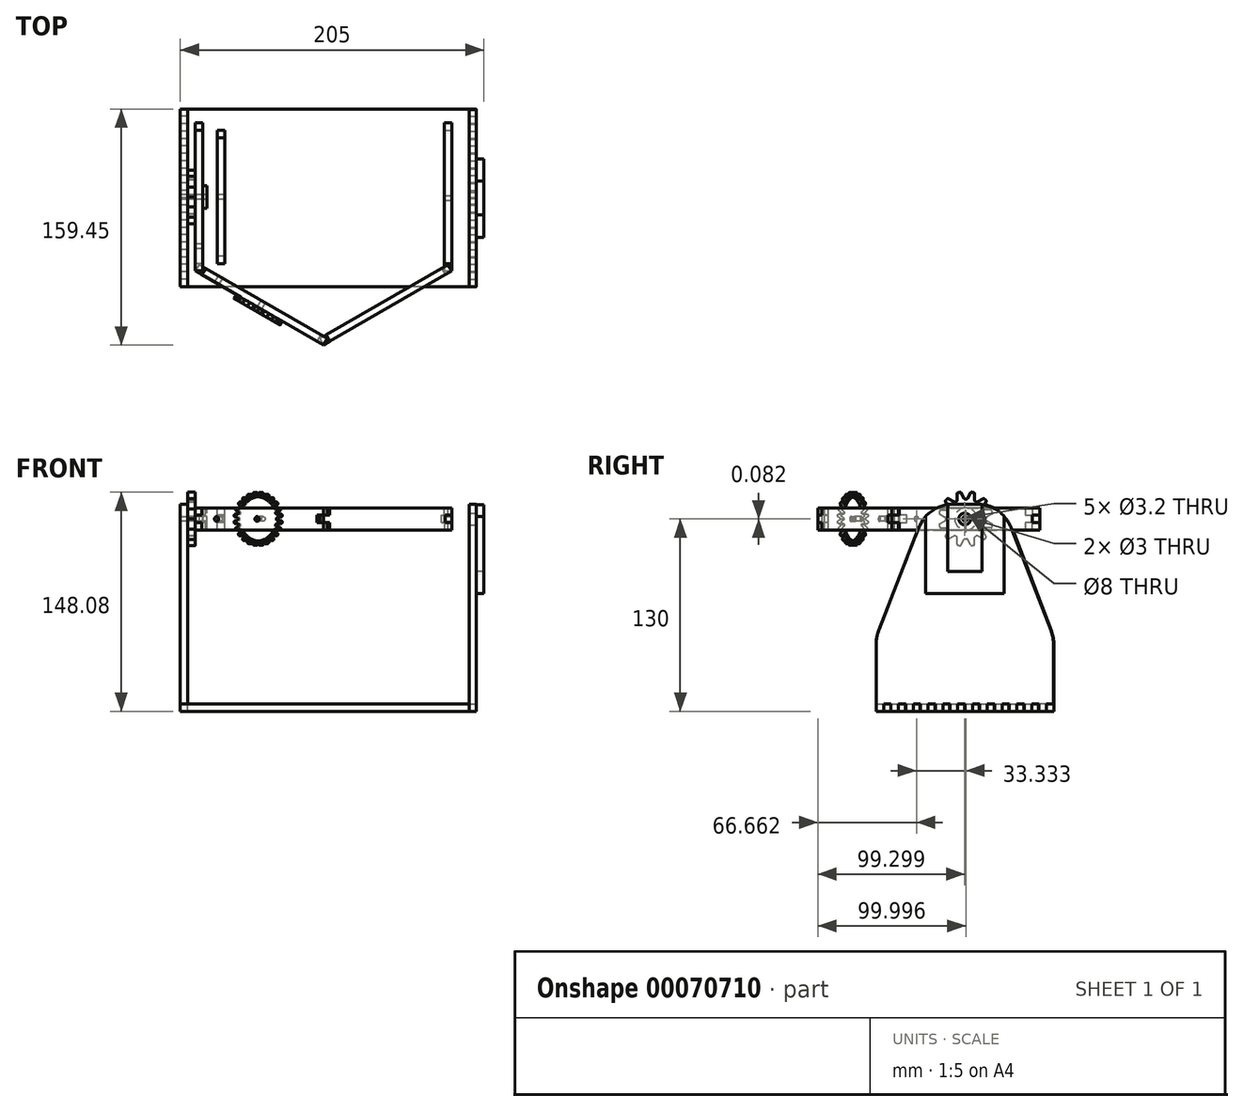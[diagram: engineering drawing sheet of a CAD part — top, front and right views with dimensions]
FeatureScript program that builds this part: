
annotation { "Feature Type Name" : "Feature", "Feature Type Description" : "" }
export const myFeature = defineFeature(function(context is Context, id is Id, definition is map)
    precondition{}
    {
        {
            var Q0;
            Q0=qCreatedBy(makeId("Top.planeOp"),FACE);
            var sketch = newSketch(context, id + "F0", { "sketchPlane" : qUnion([Q0])});
            skLineSegment(sketch, "E0.rect.bottom", {"start": v(100, 60) * mm, "end": v(-95, 60) * mm});
            skLineSegment(sketch, "E0.rect.top", {"start": v(95, -60) * mm, "end": v(-100, -60) * mm});
            skLineSegment(sketch, "E0.rect.left", {"start": v(100, 60) * mm, "end": v(100, 55) * mm});
            skLineSegment(sketch, "E0.rect.right", {"start": v(-100, 55) * mm, "end": v(-100, 50) * mm});
            skPoint(sketch, "E0.rect.middle", {"position": v(0, 0) * mm});
            skLineSegment(sketch, "E1.bottom", {"start": v(100, 55) * mm, "end": v(95, 55) * mm});
            skLineSegment(sketch, "E1.top", {"start": v(100, 50) * mm, "end": v(95, 50) * mm});
            skLineSegment(sketch, "E1.right", {"start": v(95, 55) * mm, "end": v(95, 50) * mm});
            skLineSegment(sketch, "E2.0.1.0", {"start": v(100, 45) * mm, "end": v(95, 45) * mm});
            skLineSegment(sketch, "E2.0.1.1", {"start": v(95, 45) * mm, "end": v(95, 40) * mm});
            skLineSegment(sketch, "E2.0.1.2", {"start": v(100, 40) * mm, "end": v(95, 40) * mm});
            skLineSegment(sketch, "E2.0.2.0", {"start": v(100, 35) * mm, "end": v(95, 35) * mm});
            skLineSegment(sketch, "E2.0.2.1", {"start": v(95, 35) * mm, "end": v(95, 30) * mm});
            skLineSegment(sketch, "E2.0.2.2", {"start": v(100, 30) * mm, "end": v(95, 30) * mm});
            skLineSegment(sketch, "E2.0.3.0", {"start": v(100, 25) * mm, "end": v(95, 25) * mm});
            skLineSegment(sketch, "E2.0.3.1", {"start": v(95, 25) * mm, "end": v(95, 20) * mm});
            skLineSegment(sketch, "E2.0.3.2", {"start": v(100, 20) * mm, "end": v(95, 20) * mm});
            skLineSegment(sketch, "E2.0.4.0", {"start": v(100, 15) * mm, "end": v(95, 15) * mm});
            skLineSegment(sketch, "E2.0.4.1", {"start": v(95, 15) * mm, "end": v(95, 10) * mm});
            skLineSegment(sketch, "E2.0.4.2", {"start": v(100, 10) * mm, "end": v(95, 10) * mm});
            skLineSegment(sketch, "E2.0.5.0", {"start": v(100, 5) * mm, "end": v(95, 5) * mm});
            skLineSegment(sketch, "E2.0.5.1", {"start": v(95, 5) * mm, "end": v(95, 0) * mm});
            skLineSegment(sketch, "E2.0.5.2", {"start": v(100, 0) * mm, "end": v(95, 0) * mm});
            skLineSegment(sketch, "E2.0.6.0", {"start": v(100, -5) * mm, "end": v(95, -5) * mm});
            skLineSegment(sketch, "E2.0.6.1", {"start": v(95, -5) * mm, "end": v(95, -10) * mm});
            skLineSegment(sketch, "E2.0.6.2", {"start": v(100, -10) * mm, "end": v(95, -10) * mm});
            skLineSegment(sketch, "E2.0.7.0", {"start": v(100, -15) * mm, "end": v(95, -15) * mm});
            skLineSegment(sketch, "E2.0.7.1", {"start": v(95, -15) * mm, "end": v(95, -20) * mm});
            skLineSegment(sketch, "E2.0.7.2", {"start": v(100, -20) * mm, "end": v(95, -20) * mm});
            skLineSegment(sketch, "E2.0.8.0", {"start": v(100, -25) * mm, "end": v(95, -25) * mm});
            skLineSegment(sketch, "E2.0.8.1", {"start": v(95, -25) * mm, "end": v(95, -30) * mm});
            skLineSegment(sketch, "E2.0.8.2", {"start": v(100, -30) * mm, "end": v(95, -30) * mm});
            skLineSegment(sketch, "E2.0.9.0", {"start": v(100, -35) * mm, "end": v(95, -35) * mm});
            skLineSegment(sketch, "E2.0.9.1", {"start": v(95, -35) * mm, "end": v(95, -40) * mm});
            skLineSegment(sketch, "E2.0.9.2", {"start": v(100, -40) * mm, "end": v(95, -40) * mm});
            skLineSegment(sketch, "E2.0.10.0", {"start": v(100, -45) * mm, "end": v(95, -45) * mm});
            skLineSegment(sketch, "E2.0.10.1", {"start": v(95, -45) * mm, "end": v(95, -50) * mm});
            skLineSegment(sketch, "E2.0.10.2", {"start": v(100, -50) * mm, "end": v(95, -50) * mm});
            skLineSegment(sketch, "E2.0.11.0", {"start": v(100, -55) * mm, "end": v(95, -55) * mm});
            skLineSegment(sketch, "E2.0.11.1", {"start": v(95, -55) * mm, "end": v(95, -60) * mm});
            skLineSegment(sketch, "E2.direction1", {"start": v(95, 55) * mm, "end": v(119, 55) * mm, "construction": true});
            skLineSegment(sketch, "E2.direction2", {"start": v(95, 55) * mm, "end": v(95, 45) * mm, "construction": true});
            skLineSegment(sketch, "E3", {"start": v(0, -60) * mm, "end": v(0, 60) * mm, "construction": true});
            skLineSegment(sketch, "E4.1.0", {"start": v(-100, -30) * mm, "end": v(-95, -30) * mm});
            skLineSegment(sketch, "E4.1.1", {"start": v(-100, 15) * mm, "end": v(-95, 15) * mm});
            skLineSegment(sketch, "E4.1.2", {"start": v(-95, -35) * mm, "end": v(-95, -30) * mm});
            skLineSegment(sketch, "E4.1.3", {"start": v(-100, 30) * mm, "end": v(-95, 30) * mm});
            skLineSegment(sketch, "E4.1.4", {"start": v(-100, 0) * mm, "end": v(-95, 0) * mm});
            skLineSegment(sketch, "E4.1.5", {"start": v(-100, 55) * mm, "end": v(-95, 55) * mm});
            skLineSegment(sketch, "E4.1.6", {"start": v(-95, 55) * mm, "end": v(-95, 60) * mm});
            skLineSegment(sketch, "E4.1.7", {"start": v(-100, -25) * mm, "end": v(-95, -25) * mm});
            skLineSegment(sketch, "E4.1.8", {"start": v(-100, 5) * mm, "end": v(-95, 5) * mm});
            skLineSegment(sketch, "E4.1.9", {"start": v(-95, -25) * mm, "end": v(-95, -20) * mm});
            skLineSegment(sketch, "E4.1.10", {"start": v(-100, 35) * mm, "end": v(-95, 35) * mm});
            skLineSegment(sketch, "E4.1.11", {"start": v(-100, -20) * mm, "end": v(-95, -20) * mm});
            skLineSegment(sketch, "E4.1.12", {"start": v(-100, -35) * mm, "end": v(-95, -35) * mm});
            skLineSegment(sketch, "E4.1.13", {"start": v(-100, -40) * mm, "end": v(-95, -40) * mm});
            skLineSegment(sketch, "E4.1.14", {"start": v(-95, -45) * mm, "end": v(-95, -40) * mm});
            skLineSegment(sketch, "E4.1.15", {"start": v(-95, -55) * mm, "end": v(-95, -50) * mm});
            skLineSegment(sketch, "E4.1.16", {"start": v(-95, 25) * mm, "end": v(-95, 30) * mm});
            skLineSegment(sketch, "E4.1.17", {"start": v(-100, 50) * mm, "end": v(-95, 50) * mm});
            skLineSegment(sketch, "E4.1.18", {"start": v(-95, -5) * mm, "end": v(-95, 0) * mm});
            skLineSegment(sketch, "E4.1.19", {"start": v(-100, 20) * mm, "end": v(-95, 20) * mm});
            skLineSegment(sketch, "E4.1.20", {"start": v(-95, 45) * mm, "end": v(-95, 50) * mm});
            skLineSegment(sketch, "E4.1.21", {"start": v(-100, 25) * mm, "end": v(-95, 25) * mm});
            skLineSegment(sketch, "E4.1.22", {"start": v(-100, 40) * mm, "end": v(-95, 40) * mm});
            skLineSegment(sketch, "E4.1.23", {"start": v(-100, -5) * mm, "end": v(-95, -5) * mm});
            skLineSegment(sketch, "E4.1.24", {"start": v(-95, 15) * mm, "end": v(-95, 20) * mm});
            skLineSegment(sketch, "E4.1.25", {"start": v(-95, -15) * mm, "end": v(-95, -10) * mm});
            skLineSegment(sketch, "E4.1.26", {"start": v(-100, 10) * mm, "end": v(-95, 10) * mm});
            skLineSegment(sketch, "E4.1.27", {"start": v(-95, 35) * mm, "end": v(-95, 40) * mm});
            skLineSegment(sketch, "E4.1.28", {"start": v(-100, 45) * mm, "end": v(-95, 45) * mm});
            skLineSegment(sketch, "E4.1.29", {"start": v(-100, -10) * mm, "end": v(-95, -10) * mm});
            skLineSegment(sketch, "E4.1.30", {"start": v(-100, -15) * mm, "end": v(-95, -15) * mm});
            skLineSegment(sketch, "E4.1.31", {"start": v(-95, 5) * mm, "end": v(-95, 10) * mm});
            skLineSegment(sketch, "E4.1.32", {"start": v(-100, -45) * mm, "end": v(-95, -45) * mm});
            skLineSegment(sketch, "E4.1.33", {"start": v(-100, -50) * mm, "end": v(-95, -50) * mm});
            skLineSegment(sketch, "E4.1.35", {"start": v(-100, -55) * mm, "end": v(-95, -55) * mm});
            skLineSegment(sketch, "E4.anchor1", {"start": v(0, 0) * mm, "end": v(95, 30) * mm, "construction": true});
            skLineSegment(sketch, "E4.anchor2", {"start": v(0, 0) * mm, "end": v(-95, -30) * mm, "construction": true});
            skLineSegment(sketch, "E5.trimOffspring", {"start": v(100, 50) * mm, "end": v(100, 45) * mm});
            skLineSegment(sketch, "E6.trimOffspring", {"start": v(100, 40) * mm, "end": v(100, 35) * mm});
            skLineSegment(sketch, "E7.trimOffspring", {"start": v(100, 30) * mm, "end": v(100, 25) * mm});
            skLineSegment(sketch, "E8.trimOffspring", {"start": v(100, 20) * mm, "end": v(100, 15) * mm});
            skLineSegment(sketch, "E9.trimOffspring", {"start": v(100, 10) * mm, "end": v(100, 5) * mm});
            skLineSegment(sketch, "E10.trimOffspring", {"start": v(100, 0) * mm, "end": v(100, -5) * mm});
            skLineSegment(sketch, "E11.trimOffspring", {"start": v(100, -10) * mm, "end": v(100, -15) * mm});
            skLineSegment(sketch, "E12.trimOffspring", {"start": v(100, -20) * mm, "end": v(100, -25) * mm});
            skLineSegment(sketch, "E13.trimOffspring", {"start": v(100, -30) * mm, "end": v(100, -35) * mm});
            skLineSegment(sketch, "E14.trimOffspring", {"start": v(100, -40) * mm, "end": v(100, -45) * mm});
            skLineSegment(sketch, "E15.trimOffspring", {"start": v(100, -50) * mm, "end": v(100, -55) * mm});
            skPoint(sketch, "E16.orphan", {"position": v(100, -60) * mm});
            skPoint(sketch, "E17.orphan", {"position": v(-100, 60) * mm});
            skLineSegment(sketch, "E18.trimOffspring", {"start": v(-100, 45) * mm, "end": v(-100, 40) * mm});
            skLineSegment(sketch, "E19.trimOffspring", {"start": v(-100, 35) * mm, "end": v(-100, 30) * mm});
            skLineSegment(sketch, "E20.trimOffspring", {"start": v(-100, 25) * mm, "end": v(-100, 20) * mm});
            skLineSegment(sketch, "E21.trimOffspring", {"start": v(-100, 15) * mm, "end": v(-100, 10) * mm});
            skLineSegment(sketch, "E22.trimOffspring", {"start": v(-100, 5) * mm, "end": v(-100, 0) * mm});
            skLineSegment(sketch, "E23.trimOffspring", {"start": v(-100, -5) * mm, "end": v(-100, -10) * mm});
            skLineSegment(sketch, "E24.trimOffspring", {"start": v(-100, -15) * mm, "end": v(-100, -20) * mm});
            skLineSegment(sketch, "E25.trimOffspring", {"start": v(-100, -55) * mm, "end": v(-100, -60) * mm});
            skLineSegment(sketch, "E26.trimOffspring", {"start": v(-100, -45) * mm, "end": v(-100, -50) * mm});
            skLineSegment(sketch, "E27.trimOffspring", {"start": v(-100, -35) * mm, "end": v(-100, -40) * mm});
            skLineSegment(sketch, "E28.trimOffspring", {"start": v(-100, -25) * mm, "end": v(-100, -30) * mm});
            skSolve(sketch);
        }
        {
            var Q0;
            Q0=makeQuery(id+"F0.imprint","IMPRINT",FACE,{"disambiguationData":[TD([[makeQuery(id+"F0.imprint","IMPRINT",EDGE,{"derivedFrom":sQuery(id+"F0.wireOp",EDGE,"E0.rect.bottom")}),1.0]])]});
            extrude(context, id + "F1", {"entities" : qUnion([Q0]), "depth" : 5 * mm});
        }
        {
            var Q0;
            Q0=makeQuery(id+"F1.opExtrude","SWEPT_FACE",FACE,{"disambiguationData":[OSD([sQuery(id+"F0.wireOp",EDGE,"E5.trimOffspring")])]});
            var sketch = newSketch(context, id + "F2", { "sketchPlane" : qUnion([Q0])});
            skLineSegment(sketch, "E29.bottom", {"start": v(55, 0) * mm, "end": v(49.7, 0) * mm});
            skLineSegment(sketch, "E29.top", {"start": v(59.7, 140) * mm, "end": v(-60, 140) * mm, "construction": true});
            skLineSegment(sketch, "E29.left", {"start": v(59.7, 5) * mm, "end": v(59.7, 140) * mm, "construction": true});
            skLineSegment(sketch, "E29.right", {"start": v(-60, 0) * mm, "end": v(-60, 140) * mm, "construction": true});
            skLineSegment(sketch, "E30", {"start": v(-58.31, 54.36) * mm, "end": v(-31.34, 124.03) * mm});
            skLineSegment(sketch, "E31", {"start": v(-8.02, 140) * mm, "end": v(7.72, 140) * mm});
            skLineSegment(sketch, "E32", {"start": v(31.03, 124.03) * mm, "end": v(58.01, 54.36) * mm});
            skLineSegment(sketch, "E33", {"start": v(59.7, 45.33) * mm, "end": v(59.7, 5) * mm});
            skLineSegment(sketch, "E34", {"start": v(-60, 45.33) * mm, "end": v(-60, 0) * mm});
            skPoint(sketch, "E35", {"position": v(-0.15, 140) * mm});
            skPoint(sketch, "E36.visualSharp", {"position": v(-25.15, 140) * mm});
            skArc(sketch, "E36.filletArc", {"start": v(-8.02, 140) * mm, "mid": v(-22.15, 135.62) * mm, "end": v(-31.34, 124.03) * mm});
            skPoint(sketch, "E37.visualSharp", {"position": v(-60, 50) * mm});
            skArc(sketch, "E37.filletArc", {"start": v(-58.31, 54.36) * mm, "mid": v(-59.57, 49.92) * mm, "end": v(-60, 45.33) * mm});
            skPoint(sketch, "E38.visualSharp", {"position": v(24.85, 140) * mm});
            skArc(sketch, "E38.filletArc", {"start": v(31.03, 124.03) * mm, "mid": v(21.85, 135.62) * mm, "end": v(7.72, 140) * mm});
            skPoint(sketch, "E39.visualSharp", {"position": v(59.7, 50) * mm});
            skArc(sketch, "E39.filletArc", {"start": v(59.7, 45.33) * mm, "mid": v(59.27, 49.92) * mm, "end": v(58.01, 54.36) * mm});
            skLineSegment(sketch, "E40", {"start": v(-0.15, 140) * mm, "end": v(-0.15, 130) * mm, "construction": true});
            skCircle(sketch, "E41", {"center": v(-0.15, 130) * mm, "radius": 4 * mm});
            skLineSegment(sketch, "E42.top", {"start": v(59.7, 5) * mm, "end": v(55, 5) * mm});
            skLineSegment(sketch, "E42.right", {"start": v(55, 0) * mm, "end": v(55, 5) * mm});
            skLineSegment(sketch, "E43.1.0.0", {"start": v(45, 0) * mm, "end": v(45, 5) * mm});
            skLineSegment(sketch, "E43.1.0.1", {"start": v(49.7, 5) * mm, "end": v(45, 5) * mm});
            skLineSegment(sketch, "E43.1.0.2", {"start": v(49.7, 0) * mm, "end": v(49.7, 5) * mm});
            skLineSegment(sketch, "E43.2.0.0", {"start": v(35, 0) * mm, "end": v(35, 5) * mm});
            skLineSegment(sketch, "E43.2.0.1", {"start": v(39.7, 5) * mm, "end": v(35, 5) * mm});
            skLineSegment(sketch, "E43.2.0.2", {"start": v(39.7, 0) * mm, "end": v(39.7, 5) * mm});
            skLineSegment(sketch, "E43.3.0.0", {"start": v(25, 0) * mm, "end": v(25, 5) * mm});
            skLineSegment(sketch, "E43.3.0.1", {"start": v(29.7, 5) * mm, "end": v(25, 5) * mm});
            skLineSegment(sketch, "E43.3.0.2", {"start": v(29.7, 0) * mm, "end": v(29.7, 5) * mm});
            skLineSegment(sketch, "E43.4.0.0", {"start": v(15, 0) * mm, "end": v(15, 5) * mm});
            skLineSegment(sketch, "E43.4.0.1", {"start": v(19.7, 5) * mm, "end": v(15, 5) * mm});
            skLineSegment(sketch, "E43.4.0.2", {"start": v(19.7, 0) * mm, "end": v(19.7, 5) * mm});
            skLineSegment(sketch, "E43.5.0.0", {"start": v(5, 0) * mm, "end": v(5, 5) * mm});
            skLineSegment(sketch, "E43.5.0.1", {"start": v(9.7, 5) * mm, "end": v(5, 5) * mm});
            skLineSegment(sketch, "E43.5.0.2", {"start": v(9.7, 0) * mm, "end": v(9.7, 5) * mm});
            skLineSegment(sketch, "E43.6.0.0", {"start": v(-5, 0) * mm, "end": v(-5, 5) * mm});
            skLineSegment(sketch, "E43.6.0.1", {"start": v(-0.3, 5) * mm, "end": v(-5, 5) * mm});
            skLineSegment(sketch, "E43.6.0.2", {"start": v(-0.3, 0) * mm, "end": v(-0.3, 5) * mm});
            skLineSegment(sketch, "E43.7.0.0", {"start": v(-15, 0) * mm, "end": v(-15, 5) * mm});
            skLineSegment(sketch, "E43.7.0.1", {"start": v(-10.3, 5) * mm, "end": v(-15, 5) * mm});
            skLineSegment(sketch, "E43.7.0.2", {"start": v(-10.3, 0) * mm, "end": v(-10.3, 5) * mm});
            skLineSegment(sketch, "E43.8.0.0", {"start": v(-25, 0) * mm, "end": v(-25, 5) * mm});
            skLineSegment(sketch, "E43.8.0.1", {"start": v(-20.3, 5) * mm, "end": v(-25, 5) * mm});
            skLineSegment(sketch, "E43.8.0.2", {"start": v(-20.3, 0) * mm, "end": v(-20.3, 5) * mm});
            skLineSegment(sketch, "E43.9.0.0", {"start": v(-35, 0) * mm, "end": v(-35, 5) * mm});
            skLineSegment(sketch, "E43.9.0.1", {"start": v(-30.3, 5) * mm, "end": v(-35, 5) * mm});
            skLineSegment(sketch, "E43.9.0.2", {"start": v(-30.3, 0) * mm, "end": v(-30.3, 5) * mm});
            skLineSegment(sketch, "E43.10.0.0", {"start": v(-45, 0) * mm, "end": v(-45, 5) * mm});
            skLineSegment(sketch, "E43.10.0.1", {"start": v(-40.3, 5) * mm, "end": v(-45, 5) * mm});
            skLineSegment(sketch, "E43.10.0.2", {"start": v(-40.3, 0) * mm, "end": v(-40.3, 5) * mm});
            skLineSegment(sketch, "E43.11.0.0", {"start": v(-55, 0) * mm, "end": v(-55, 5) * mm});
            skLineSegment(sketch, "E43.11.0.1", {"start": v(-50.3, 5) * mm, "end": v(-55, 5) * mm});
            skLineSegment(sketch, "E43.11.0.2", {"start": v(-50.3, 0) * mm, "end": v(-50.3, 5) * mm});
            skLineSegment(sketch, "E43.direction1", {"start": v(55, 0) * mm, "end": v(45, 0) * mm, "construction": true});
            skLineSegment(sketch, "E44.trimOffspring", {"start": v(45, 0) * mm, "end": v(39.7, 0) * mm});
            skLineSegment(sketch, "E45.trimOffspring", {"start": v(35, 0) * mm, "end": v(29.7, 0) * mm});
            skLineSegment(sketch, "E46.trimOffspring", {"start": v(25, 0) * mm, "end": v(19.7, 0) * mm});
            skLineSegment(sketch, "E47.trimOffspring", {"start": v(15, 0) * mm, "end": v(9.7, 0) * mm});
            skLineSegment(sketch, "E48.trimOffspring", {"start": v(5, 0) * mm, "end": v(-0.3, 0) * mm});
            skLineSegment(sketch, "E49.trimOffspring", {"start": v(-5, 0) * mm, "end": v(-10.3, 0) * mm});
            skLineSegment(sketch, "E50.trimOffspring", {"start": v(-15, 0) * mm, "end": v(-20.3, 0) * mm});
            skLineSegment(sketch, "E51.trimOffspring", {"start": v(-25, 0) * mm, "end": v(-30.3, 0) * mm});
            skLineSegment(sketch, "E52.trimOffspring", {"start": v(-35, 0) * mm, "end": v(-40.3, 0) * mm});
            skLineSegment(sketch, "E53.trimOffspring", {"start": v(-45, 0) * mm, "end": v(-50.3, 0) * mm});
            skLineSegment(sketch, "E54.trimOffspring", {"start": v(-55, 0) * mm, "end": v(-60, 0) * mm});
            skLineSegment(sketch, "E55.rect.bottom", {"start": v(14.85, 101.5) * mm, "end": v(-15.15, 101.5) * mm, "construction": true});
            skLineSegment(sketch, "E55.rect.top", {"start": v(14.85, 106.5) * mm, "end": v(-15.15, 106.5) * mm, "construction": true});
            skLineSegment(sketch, "E55.rect.left", {"start": v(14.85, 101.5) * mm, "end": v(14.85, 106.5) * mm, "construction": true});
            skLineSegment(sketch, "E55.rect.right", {"start": v(-15.15, 101.5) * mm, "end": v(-15.15, 106.5) * mm, "construction": true});
            skPoint(sketch, "E55.rect.middle", {"position": v(-0.15, 104) * mm});
            skSolve(sketch);
        }
        {
            var Q0;
            Q0=qSketchRegion(id+"F2",true);
            extrude(context, id + "F3", {"entities" : qUnion([Q0]), "oppositeDirection" : true, "depth" : 5 * mm});
        }
        {
            var Q0;
            Q0=makeQuery(id+"F1.opExtrude","SWEPT_FACE",FACE,{"disambiguationData":[OSD([sQuery(id+"F0.wireOp",EDGE,"E0.rect.right")])]});
            var sketch = newSketch(context, id + "F4", { "sketchPlane" : qUnion([Q0])});
            skLineSegment(sketch, "E56.bottom", {"start": v(55, 0) * mm, "end": v(50, 0) * mm});
            skLineSegment(sketch, "E56.top", {"start": v(60, 140) * mm, "end": v(-60, 140) * mm, "construction": true});
            skLineSegment(sketch, "E56.left", {"start": v(60, 5) * mm, "end": v(60, 140) * mm, "construction": true});
            skLineSegment(sketch, "E56.right", {"start": v(-60, 0) * mm, "end": v(-60, 140) * mm, "construction": true});
            skLineSegment(sketch, "E57", {"start": v(-60, 0) * mm, "end": v(-60, 45.4) * mm});
            skLineSegment(sketch, "E58", {"start": v(-58.36, 54.3) * mm, "end": v(-31.83, 123.9) * mm});
            skLineSegment(sketch, "E59", {"start": v(-8.47, 140) * mm, "end": v(7.37, 140) * mm});
            skLineSegment(sketch, "E60", {"start": v(30.6, 124.27) * mm, "end": v(58.22, 55.1) * mm});
            skLineSegment(sketch, "E61", {"start": v(60, 45.82) * mm, "end": v(60, 5) * mm});
            skPoint(sketch, "E62.visualSharp", {"position": v(-60, 50) * mm});
            skArc(sketch, "E62.filletArc", {"start": v(-58.36, 54.3) * mm, "mid": v(-59.59, 49.92) * mm, "end": v(-60, 45.4) * mm});
            skPoint(sketch, "E63.visualSharp", {"position": v(-25.69, 140) * mm});
            skArc(sketch, "E63.filletArc", {"start": v(-8.47, 140) * mm, "mid": v(-22.65, 135.59) * mm, "end": v(-31.83, 123.9) * mm});
            skPoint(sketch, "E64.visualSharp", {"position": v(24.31, 140) * mm});
            skArc(sketch, "E64.filletArc", {"start": v(30.6, 124.27) * mm, "mid": v(21.4, 135.7) * mm, "end": v(7.37, 140) * mm});
            skPoint(sketch, "E65.visualSharp", {"position": v(60, 50.63) * mm});
            skArc(sketch, "E65.filletArc", {"start": v(60, 45.82) * mm, "mid": v(59.55, 50.54) * mm, "end": v(58.22, 55.1) * mm});
            skLineSegment(sketch, "E66", {"start": v(-0.55, 140) * mm, "end": v(-0.55, 130) * mm, "construction": true});
            skPoint(sketch, "E66.endSnap0", {"position": v(-0.55, 140) * mm});
            skCircle(sketch, "E67", {"center": v(-0.55, 130) * mm, "radius": 1.5 * mm});
            skLineSegment(sketch, "E68.top", {"start": v(60, 5) * mm, "end": v(55, 5) * mm});
            skLineSegment(sketch, "E68.right", {"start": v(55, 0) * mm, "end": v(55, 5) * mm});
            skLineSegment(sketch, "E69.1.0.0", {"start": v(45, 0) * mm, "end": v(45, 5) * mm});
            skLineSegment(sketch, "E69.1.0.1", {"start": v(50, 5) * mm, "end": v(45, 5) * mm});
            skLineSegment(sketch, "E69.1.0.2", {"start": v(50, 0) * mm, "end": v(50, 5) * mm});
            skLineSegment(sketch, "E69.2.0.0", {"start": v(35, 0) * mm, "end": v(35, 5) * mm});
            skLineSegment(sketch, "E69.2.0.1", {"start": v(40, 5) * mm, "end": v(35, 5) * mm});
            skLineSegment(sketch, "E69.2.0.2", {"start": v(40, 0) * mm, "end": v(40, 5) * mm});
            skLineSegment(sketch, "E69.3.0.0", {"start": v(25, 0) * mm, "end": v(25, 5) * mm});
            skLineSegment(sketch, "E69.3.0.1", {"start": v(30, 5) * mm, "end": v(25, 5) * mm});
            skLineSegment(sketch, "E69.3.0.2", {"start": v(30, 0) * mm, "end": v(30, 5) * mm});
            skLineSegment(sketch, "E69.4.0.0", {"start": v(15, 0) * mm, "end": v(15, 5) * mm});
            skLineSegment(sketch, "E69.4.0.1", {"start": v(20, 5) * mm, "end": v(15, 5) * mm});
            skLineSegment(sketch, "E69.4.0.2", {"start": v(20, 0) * mm, "end": v(20, 5) * mm});
            skLineSegment(sketch, "E69.5.0.0", {"start": v(5, 0) * mm, "end": v(5, 5) * mm});
            skLineSegment(sketch, "E69.5.0.1", {"start": v(10, 5) * mm, "end": v(5, 5) * mm});
            skLineSegment(sketch, "E69.5.0.2", {"start": v(10, 0) * mm, "end": v(10, 5) * mm});
            skLineSegment(sketch, "E69.6.0.0", {"start": v(-5, 0) * mm, "end": v(-5, 5) * mm});
            skLineSegment(sketch, "E69.6.0.1", {"start": v(0, 5) * mm, "end": v(-5, 5) * mm});
            skLineSegment(sketch, "E69.6.0.2", {"start": v(0, 0) * mm, "end": v(0, 5) * mm});
            skLineSegment(sketch, "E69.7.0.0", {"start": v(-15, 0) * mm, "end": v(-15, 5) * mm});
            skLineSegment(sketch, "E69.7.0.1", {"start": v(-10, 5) * mm, "end": v(-15, 5) * mm});
            skLineSegment(sketch, "E69.7.0.2", {"start": v(-10, 0) * mm, "end": v(-10, 5) * mm});
            skLineSegment(sketch, "E69.8.0.0", {"start": v(-25, 0) * mm, "end": v(-25, 5) * mm});
            skLineSegment(sketch, "E69.8.0.1", {"start": v(-20, 5) * mm, "end": v(-25, 5) * mm});
            skLineSegment(sketch, "E69.8.0.2", {"start": v(-20, 0) * mm, "end": v(-20, 5) * mm});
            skLineSegment(sketch, "E69.9.0.0", {"start": v(-35, 0) * mm, "end": v(-35, 5) * mm});
            skLineSegment(sketch, "E69.9.0.1", {"start": v(-30, 5) * mm, "end": v(-35, 5) * mm});
            skLineSegment(sketch, "E69.9.0.2", {"start": v(-30, 0) * mm, "end": v(-30, 5) * mm});
            skLineSegment(sketch, "E69.10.0.0", {"start": v(-45, 0) * mm, "end": v(-45, 5) * mm});
            skLineSegment(sketch, "E69.10.0.1", {"start": v(-40, 5) * mm, "end": v(-45, 5) * mm});
            skLineSegment(sketch, "E69.10.0.2", {"start": v(-40, 0) * mm, "end": v(-40, 5) * mm});
            skLineSegment(sketch, "E69.11.0.0", {"start": v(-55, 0) * mm, "end": v(-55, 5) * mm});
            skLineSegment(sketch, "E69.11.0.1", {"start": v(-50, 5) * mm, "end": v(-55, 5) * mm});
            skLineSegment(sketch, "E69.11.0.2", {"start": v(-50, 0) * mm, "end": v(-50, 5) * mm});
            skLineSegment(sketch, "E69.direction1", {"start": v(55, 0) * mm, "end": v(45, 0) * mm, "construction": true});
            skLineSegment(sketch, "E70.trimOffspring", {"start": v(45, 0) * mm, "end": v(40, 0) * mm});
            skLineSegment(sketch, "E71.trimOffspring", {"start": v(35, 0) * mm, "end": v(30, 0) * mm});
            skLineSegment(sketch, "E72.trimOffspring", {"start": v(25, 0) * mm, "end": v(20, 0) * mm});
            skLineSegment(sketch, "E73.trimOffspring", {"start": v(15, 0) * mm, "end": v(10, 0) * mm});
            skLineSegment(sketch, "E74.trimOffspring", {"start": v(5, 0) * mm, "end": v(0, 0) * mm});
            skLineSegment(sketch, "E75.trimOffspring", {"start": v(-5, 0) * mm, "end": v(-10, 0) * mm});
            skLineSegment(sketch, "E76.trimOffspring", {"start": v(-15, 0) * mm, "end": v(-20, 0) * mm});
            skLineSegment(sketch, "E77.trimOffspring", {"start": v(-25, 0) * mm, "end": v(-30, 0) * mm});
            skLineSegment(sketch, "E78.trimOffspring", {"start": v(-35, 0) * mm, "end": v(-40, 0) * mm});
            skLineSegment(sketch, "E79.trimOffspring", {"start": v(-45, 0) * mm, "end": v(-50, 0) * mm});
            skLineSegment(sketch, "E80.trimOffspring", {"start": v(-55, 0) * mm, "end": v(-60, 0) * mm});
            skSolve(sketch);
        }
        {
            var Q0;
            Q0=qSketchRegion(id+"F4",true);
            extrude(context, id + "F5", {"entities" : qUnion([Q0]), "oppositeDirection" : true, "depth" : 5 * mm});
        }
        {
            var Q0;
            Q0=makeQuery(id+"F5.opExtrude","CAP_FACE",FACE,{"disambiguationData":[OSD([sQuery(id+"F4.wireOp",EDGE,"E56.bottom"),sQuery(id+"F4.wireOp",EDGE,"E57"),sQuery(id+"F4.wireOp",EDGE,"E58"),sQuery(id+"F4.wireOp",EDGE,"E59"),sQuery(id+"F4.wireOp",EDGE,"E60"),sQuery(id+"F4.wireOp",EDGE,"E61"),sQuery(id+"F4.wireOp",EDGE,"E62.filletArc"),sQuery(id+"F4.wireOp",EDGE,"E63.filletArc"),sQuery(id+"F4.wireOp",EDGE,"E64.filletArc"),sQuery(id+"F4.wireOp",EDGE,"E65.filletArc"),sQuery(id+"F4.wireOp",EDGE,"E67"),sQuery(id+"F4.wireOp",EDGE,"E68.top"),sQuery(id+"F4.wireOp",EDGE,"E68.right"),sQuery(id+"F4.wireOp",EDGE,"E69.1.0.0"),sQuery(id+"F4.wireOp",EDGE,"E69.1.0.1"),sQuery(id+"F4.wireOp",EDGE,"E69.1.0.2"),sQuery(id+"F4.wireOp",EDGE,"E69.2.0.0"),sQuery(id+"F4.wireOp",EDGE,"E69.2.0.1"),sQuery(id+"F4.wireOp",EDGE,"E69.2.0.2"),sQuery(id+"F4.wireOp",EDGE,"E69.3.0.0"),sQuery(id+"F4.wireOp",EDGE,"E69.3.0.1"),sQuery(id+"F4.wireOp",EDGE,"E69.3.0.2"),sQuery(id+"F4.wireOp",EDGE,"E69.4.0.0"),sQuery(id+"F4.wireOp",EDGE,"E69.4.0.1"),sQuery(id+"F4.wireOp",EDGE,"E69.4.0.2"),sQuery(id+"F4.wireOp",EDGE,"E69.5.0.0"),sQuery(id+"F4.wireOp",EDGE,"E69.5.0.1"),sQuery(id+"F4.wireOp",EDGE,"E69.5.0.2"),sQuery(id+"F4.wireOp",EDGE,"E69.6.0.0"),sQuery(id+"F4.wireOp",EDGE,"E69.6.0.1"),sQuery(id+"F4.wireOp",EDGE,"E69.6.0.2"),sQuery(id+"F4.wireOp",EDGE,"E69.7.0.0"),sQuery(id+"F4.wireOp",EDGE,"E69.7.0.1"),sQuery(id+"F4.wireOp",EDGE,"E69.7.0.2"),sQuery(id+"F4.wireOp",EDGE,"E69.8.0.0"),sQuery(id+"F4.wireOp",EDGE,"E69.8.0.1"),sQuery(id+"F4.wireOp",EDGE,"E69.8.0.2"),sQuery(id+"F4.wireOp",EDGE,"E69.9.0.0"),sQuery(id+"F4.wireOp",EDGE,"E69.9.0.1"),sQuery(id+"F4.wireOp",EDGE,"E69.9.0.2"),sQuery(id+"F4.wireOp",EDGE,"E69.10.0.0"),sQuery(id+"F4.wireOp",EDGE,"E69.10.0.1"),sQuery(id+"F4.wireOp",EDGE,"E69.10.0.2"),sQuery(id+"F4.wireOp",EDGE,"E69.11.0.0"),sQuery(id+"F4.wireOp",EDGE,"E69.11.0.1"),sQuery(id+"F4.wireOp",EDGE,"E69.11.0.2"),sQuery(id+"F4.wireOp",EDGE,"E70.trimOffspring"),sQuery(id+"F4.wireOp",EDGE,"E71.trimOffspring"),sQuery(id+"F4.wireOp",EDGE,"E72.trimOffspring"),sQuery(id+"F4.wireOp",EDGE,"E73.trimOffspring"),sQuery(id+"F4.wireOp",EDGE,"E74.trimOffspring"),sQuery(id+"F4.wireOp",EDGE,"E75.trimOffspring"),sQuery(id+"F4.wireOp",EDGE,"E76.trimOffspring"),sQuery(id+"F4.wireOp",EDGE,"E77.trimOffspring"),sQuery(id+"F4.wireOp",EDGE,"E78.trimOffspring"),sQuery(id+"F4.wireOp",EDGE,"E79.trimOffspring"),sQuery(id+"F4.wireOp",EDGE,"E80.trimOffspring")])],"isStart":false});
            var sketch = newSketch(context, id + "F6", { "sketchPlane" : qUnion([Q0])});
            skCircle(sketch, "E81", {"center": v(0.55, 130) * mm, "radius": 13.5 * mm, "construction": true});
            skCircle(sketch, "E82", {"center": v(0.55, 130) * mm, "radius": 18.5 * mm, "construction": true});
            skCircle(sketch, "E83", {"center": v(0.55, 130) * mm, "radius": 1.6 * mm});
            skLineSegment(sketch, "E84", {"start": v(0.55, 130) * mm, "end": v(0.55, 148.5) * mm, "construction": true});
            skLineSegment(sketch, "E85", {"start": v(0.55, 130) * mm, "end": v(-8.7, 146.02) * mm, "construction": true});
            skLineSegment(sketch, "E86", {"start": v(0.55, 130) * mm, "end": v(-4.24, 147.87) * mm, "construction": true});
            skLineSegment(sketch, "E87", {"start": v(0.55, 130) * mm, "end": v(-1.87, 148.34) * mm, "construction": true});
            skLineSegment(sketch, "E88", {"start": v(0.55, 130) * mm, "end": v(-6.53, 147.1) * mm, "construction": true});
            skLineSegment(sketch, "E89", {"start": v(-0.66, 148.46) * mm, "end": v(0.55, 130) * mm, "construction": true});
            skLineSegment(sketch, "E90", {"start": v(-7.64, 146.6) * mm, "end": v(0.55, 130) * mm, "construction": true});
            skLineSegment(sketch, "E91", {"start": v(-3.06, 148.14) * mm, "end": v(0.55, 130) * mm, "construction": true});
            skLineSegment(sketch, "E92", {"start": v(-5.4, 147.52) * mm, "end": v(0.55, 130) * mm, "construction": true});
            skArc(sketch, "E93", {"start": v(-3.42, 148.07) * mm, "mid": v(-4.24, 147.87) * mm, "end": v(-5.05, 147.63) * mm});
            skLineSegment(sketch, "E94", {"start": v(-2.88, 147.83) * mm, "end": v(-0.5, 143.74) * mm});
            skLineSegment(sketch, "E95", {"start": v(-5.4, 147.16) * mm, "end": v(-5.42, 142.42) * mm});
            skLineSegment(sketch, "E96", {"start": v(-0.03, 143.5) * mm, "end": v(0.55, 143.53) * mm});
            skLineSegment(sketch, "E97", {"start": v(-5.7, 141.97) * mm, "end": v(-6.22, 141.72) * mm});
            skPoint(sketch, "E98.visualSharp", {"position": v(-0.34, 143.47) * mm});
            skArc(sketch, "E98.filletArc", {"start": v(-0.5, 143.74) * mm, "mid": v(-0.3, 143.55) * mm, "end": v(-0.03, 143.5) * mm});
            skPoint(sketch, "E99.visualSharp", {"position": v(-5.43, 142.1) * mm});
            skArc(sketch, "E99.filletArc", {"start": v(-5.7, 141.97) * mm, "mid": v(-5.5, 142.15) * mm, "end": v(-5.42, 142.42) * mm});
            skPoint(sketch, "E100.visualSharp", {"position": v(-3.06, 148.14) * mm});
            skArc(sketch, "E100.filletArc", {"start": v(-2.88, 147.83) * mm, "mid": v(-3.11, 148.04) * mm, "end": v(-3.42, 148.07) * mm});
            skPoint(sketch, "E101.visualSharp", {"position": v(-5.4, 147.52) * mm});
            skArc(sketch, "E101.filletArc", {"start": v(-5.05, 147.63) * mm, "mid": v(-5.3, 147.45) * mm, "end": v(-5.4, 147.16) * mm});
            skLineSegment(sketch, "E102.1.0", {"start": v(-6.7, 141.4) * mm, "end": v(-6.22, 141.72) * mm});
            skArc(sketch, "E102.1.1", {"start": v(-7.22, 141.38) * mm, "mid": v(-6.96, 141.31) * mm, "end": v(-6.7, 141.4) * mm});
            skLineSegment(sketch, "E102.1.2", {"start": v(-11.34, 143.73) * mm, "end": v(-7.22, 141.38) * mm});
            skArc(sketch, "E102.1.3", {"start": v(-11.34, 143.73) * mm, "mid": v(-11.64, 143.8) * mm, "end": v(-11.92, 143.67) * mm});
            skArc(sketch, "E102.1.4", {"start": v(-11.92, 143.67) * mm, "mid": v(-12.54, 143.08) * mm, "end": v(-13.12, 142.47) * mm});
            skArc(sketch, "E102.1.5", {"start": v(-13.12, 142.47) * mm, "mid": v(-13.25, 142.19) * mm, "end": v(-13.18, 141.89) * mm});
            skLineSegment(sketch, "E102.1.6", {"start": v(-13.18, 141.89) * mm, "end": v(-10.83, 137.77) * mm});
            skArc(sketch, "E102.1.7", {"start": v(-10.85, 137.24) * mm, "mid": v(-10.77, 137.5) * mm, "end": v(-10.83, 137.77) * mm});
            skLineSegment(sketch, "E102.1.8", {"start": v(-10.85, 137.24) * mm, "end": v(-11.17, 136.76) * mm});
            skLineSegment(sketch, "E102.2.0", {"start": v(-11.43, 136.25) * mm, "end": v(-11.17, 136.76) * mm});
            skArc(sketch, "E102.2.1", {"start": v(-11.87, 135.97) * mm, "mid": v(-11.6, 136.05) * mm, "end": v(-11.43, 136.25) * mm});
            skLineSegment(sketch, "E102.2.2", {"start": v(-16.61, 135.95) * mm, "end": v(-11.87, 135.97) * mm});
            skArc(sketch, "E102.2.3", {"start": v(-16.61, 135.95) * mm, "mid": v(-16.9, 135.85) * mm, "end": v(-17.09, 135.6) * mm});
            skArc(sketch, "E102.2.4", {"start": v(-17.09, 135.6) * mm, "mid": v(-17.32, 134.79) * mm, "end": v(-17.52, 133.97) * mm});
            skArc(sketch, "E102.2.5", {"start": v(-17.52, 133.97) * mm, "mid": v(-17.5, 133.66) * mm, "end": v(-17.29, 133.43) * mm});
            skLineSegment(sketch, "E102.2.6", {"start": v(-17.29, 133.43) * mm, "end": v(-13.2, 131.04) * mm});
            skArc(sketch, "E102.2.7", {"start": v(-12.95, 130.57) * mm, "mid": v(-13, 130.84) * mm, "end": v(-13.2, 131.04) * mm});
            skLineSegment(sketch, "E102.2.8", {"start": v(-12.95, 130.57) * mm, "end": v(-12.98, 130) * mm});
            skLineSegment(sketch, "E102.3.0", {"start": v(-12.95, 129.43) * mm, "end": v(-12.98, 130) * mm});
            skArc(sketch, "E102.3.1", {"start": v(-13.2, 128.96) * mm, "mid": v(-13, 129.16) * mm, "end": v(-12.95, 129.43) * mm});
            skLineSegment(sketch, "E102.3.2", {"start": v(-17.29, 126.57) * mm, "end": v(-13.2, 128.96) * mm});
            skArc(sketch, "E102.3.3", {"start": v(-17.29, 126.57) * mm, "mid": v(-17.5, 126.34) * mm, "end": v(-17.52, 126.03) * mm});
            skArc(sketch, "E102.3.4", {"start": v(-17.52, 126.03) * mm, "mid": v(-17.32, 125.21) * mm, "end": v(-17.09, 124.4) * mm});
            skArc(sketch, "E102.3.5", {"start": v(-17.09, 124.4) * mm, "mid": v(-16.9, 124.15) * mm, "end": v(-16.61, 124.05) * mm});
            skLineSegment(sketch, "E102.3.6", {"start": v(-16.61, 124.05) * mm, "end": v(-11.87, 124.03) * mm});
            skArc(sketch, "E102.3.7", {"start": v(-11.43, 123.75) * mm, "mid": v(-11.6, 123.95) * mm, "end": v(-11.87, 124.03) * mm});
            skLineSegment(sketch, "E102.3.8", {"start": v(-11.43, 123.75) * mm, "end": v(-11.17, 123.24) * mm});
            skLineSegment(sketch, "E102.4.0", {"start": v(-10.85, 122.76) * mm, "end": v(-11.17, 123.24) * mm});
            skArc(sketch, "E102.4.1", {"start": v(-10.83, 122.23) * mm, "mid": v(-10.77, 122.5) * mm, "end": v(-10.85, 122.76) * mm});
            skLineSegment(sketch, "E102.4.2", {"start": v(-13.18, 118.11) * mm, "end": v(-10.83, 122.23) * mm});
            skArc(sketch, "E102.4.3", {"start": v(-13.18, 118.11) * mm, "mid": v(-13.25, 117.81) * mm, "end": v(-13.12, 117.53) * mm});
            skArc(sketch, "E102.4.4", {"start": v(-13.12, 117.53) * mm, "mid": v(-12.54, 116.92) * mm, "end": v(-11.92, 116.33) * mm});
            skArc(sketch, "E102.4.5", {"start": v(-11.92, 116.33) * mm, "mid": v(-11.64, 116.2) * mm, "end": v(-11.34, 116.27) * mm});
            skLineSegment(sketch, "E102.4.6", {"start": v(-11.34, 116.27) * mm, "end": v(-7.22, 118.62) * mm});
            skArc(sketch, "E102.4.7", {"start": v(-6.7, 118.6) * mm, "mid": v(-6.96, 118.69) * mm, "end": v(-7.22, 118.62) * mm});
            skLineSegment(sketch, "E102.4.8", {"start": v(-6.7, 118.6) * mm, "end": v(-6.22, 118.28) * mm});
            skLineSegment(sketch, "E102.5.0", {"start": v(-5.7, 118.03) * mm, "end": v(-6.22, 118.28) * mm});
            skArc(sketch, "E102.5.1", {"start": v(-5.42, 117.58) * mm, "mid": v(-5.5, 117.85) * mm, "end": v(-5.7, 118.03) * mm});
            skLineSegment(sketch, "E102.5.2", {"start": v(-5.4, 112.84) * mm, "end": v(-5.42, 117.58) * mm});
            skArc(sketch, "E102.5.3", {"start": v(-5.4, 112.84) * mm, "mid": v(-5.3, 112.55) * mm, "end": v(-5.05, 112.37) * mm});
            skArc(sketch, "E102.5.4", {"start": v(-5.05, 112.37) * mm, "mid": v(-4.24, 112.13) * mm, "end": v(-3.42, 111.93) * mm});
            skArc(sketch, "E102.5.5", {"start": v(-3.42, 111.93) * mm, "mid": v(-3.11, 111.96) * mm, "end": v(-2.88, 112.17) * mm});
            skLineSegment(sketch, "E102.5.6", {"start": v(-2.88, 112.17) * mm, "end": v(-0.5, 116.26) * mm});
            skArc(sketch, "E102.5.7", {"start": v(-0.03, 116.5) * mm, "mid": v(-0.3, 116.45) * mm, "end": v(-0.5, 116.26) * mm});
            skLineSegment(sketch, "E102.5.8", {"start": v(-0.03, 116.5) * mm, "end": v(0.55, 116.47) * mm});
            skLineSegment(sketch, "E102.6.0", {"start": v(1.12, 116.5) * mm, "end": v(0.55, 116.47) * mm});
            skArc(sketch, "E102.6.1", {"start": v(1.58, 116.26) * mm, "mid": v(1.39, 116.45) * mm, "end": v(1.12, 116.5) * mm});
            skLineSegment(sketch, "E102.6.2", {"start": v(3.97, 112.17) * mm, "end": v(1.58, 116.26) * mm});
            skArc(sketch, "E102.6.3", {"start": v(3.97, 112.17) * mm, "mid": v(4.2, 111.96) * mm, "end": v(4.51, 111.93) * mm});
            skArc(sketch, "E102.6.4", {"start": v(4.51, 111.93) * mm, "mid": v(5.33, 112.13) * mm, "end": v(6.15, 112.37) * mm});
            skArc(sketch, "E102.6.5", {"start": v(6.15, 112.37) * mm, "mid": v(6.4, 112.55) * mm, "end": v(6.5, 112.84) * mm});
            skLineSegment(sketch, "E102.6.6", {"start": v(6.5, 112.84) * mm, "end": v(6.52, 117.58) * mm});
            skArc(sketch, "E102.6.7", {"start": v(6.8, 118.03) * mm, "mid": v(6.6, 117.85) * mm, "end": v(6.52, 117.58) * mm});
            skLineSegment(sketch, "E102.6.8", {"start": v(6.8, 118.03) * mm, "end": v(7.31, 118.28) * mm});
            skLineSegment(sketch, "E102.7.0", {"start": v(7.79, 118.6) * mm, "end": v(7.31, 118.28) * mm});
            skArc(sketch, "E102.7.1", {"start": v(8.31, 118.62) * mm, "mid": v(8.05, 118.69) * mm, "end": v(7.79, 118.6) * mm});
            skLineSegment(sketch, "E102.7.2", {"start": v(12.43, 116.27) * mm, "end": v(8.31, 118.62) * mm});
            skArc(sketch, "E102.7.3", {"start": v(12.43, 116.27) * mm, "mid": v(12.73, 116.2) * mm, "end": v(13.02, 116.33) * mm});
            skArc(sketch, "E102.7.4", {"start": v(13.02, 116.33) * mm, "mid": v(13.63, 116.92) * mm, "end": v(14.21, 117.53) * mm});
            skArc(sketch, "E102.7.5", {"start": v(14.21, 117.53) * mm, "mid": v(14.34, 117.81) * mm, "end": v(14.28, 118.11) * mm});
            skLineSegment(sketch, "E102.7.6", {"start": v(14.28, 118.11) * mm, "end": v(11.92, 122.23) * mm});
            skArc(sketch, "E102.7.7", {"start": v(11.94, 122.76) * mm, "mid": v(11.86, 122.5) * mm, "end": v(11.92, 122.23) * mm});
            skLineSegment(sketch, "E102.7.8", {"start": v(11.94, 122.76) * mm, "end": v(12.26, 123.24) * mm});
            skLineSegment(sketch, "E102.8.0", {"start": v(12.52, 123.75) * mm, "end": v(12.26, 123.24) * mm});
            skArc(sketch, "E102.8.1", {"start": v(12.96, 124.03) * mm, "mid": v(12.7, 123.95) * mm, "end": v(12.52, 123.75) * mm});
            skLineSegment(sketch, "E102.8.2", {"start": v(17.7, 124.05) * mm, "end": v(12.96, 124.03) * mm});
            skArc(sketch, "E102.8.3", {"start": v(17.7, 124.05) * mm, "mid": v(18, 124.15) * mm, "end": v(18.18, 124.4) * mm});
            skArc(sketch, "E102.8.4", {"start": v(18.18, 124.4) * mm, "mid": v(18.42, 125.21) * mm, "end": v(18.62, 126.03) * mm});
            skArc(sketch, "E102.8.5", {"start": v(18.62, 126.03) * mm, "mid": v(18.58, 126.34) * mm, "end": v(18.38, 126.57) * mm});
            skLineSegment(sketch, "E102.8.6", {"start": v(18.38, 126.57) * mm, "end": v(14.28, 128.96) * mm});
            skArc(sketch, "E102.8.7", {"start": v(14.04, 129.43) * mm, "mid": v(14.1, 129.16) * mm, "end": v(14.28, 128.96) * mm});
            skLineSegment(sketch, "E102.8.8", {"start": v(14.04, 129.43) * mm, "end": v(14.07, 130) * mm});
            skLineSegment(sketch, "E102.9.0", {"start": v(14.04, 130.57) * mm, "end": v(14.07, 130) * mm});
            skArc(sketch, "E102.9.1", {"start": v(14.28, 131.04) * mm, "mid": v(14.1, 130.84) * mm, "end": v(14.04, 130.57) * mm});
            skLineSegment(sketch, "E102.9.2", {"start": v(18.38, 133.43) * mm, "end": v(14.28, 131.04) * mm});
            skArc(sketch, "E102.9.3", {"start": v(18.38, 133.43) * mm, "mid": v(18.58, 133.66) * mm, "end": v(18.62, 133.97) * mm});
            skArc(sketch, "E102.9.4", {"start": v(18.62, 133.97) * mm, "mid": v(18.42, 134.79) * mm, "end": v(18.18, 135.6) * mm});
            skArc(sketch, "E102.9.5", {"start": v(18.18, 135.6) * mm, "mid": v(18, 135.85) * mm, "end": v(17.7, 135.95) * mm});
            skLineSegment(sketch, "E102.9.6", {"start": v(17.7, 135.95) * mm, "end": v(12.96, 135.97) * mm});
            skArc(sketch, "E102.9.7", {"start": v(12.52, 136.25) * mm, "mid": v(12.7, 136.05) * mm, "end": v(12.96, 135.97) * mm});
            skLineSegment(sketch, "E102.9.8", {"start": v(12.52, 136.25) * mm, "end": v(12.26, 136.76) * mm});
            skLineSegment(sketch, "E102.10.0", {"start": v(11.94, 137.24) * mm, "end": v(12.26, 136.76) * mm});
            skArc(sketch, "E102.10.1", {"start": v(11.92, 137.77) * mm, "mid": v(11.86, 137.5) * mm, "end": v(11.94, 137.24) * mm});
            skLineSegment(sketch, "E102.10.2", {"start": v(14.28, 141.89) * mm, "end": v(11.92, 137.77) * mm});
            skArc(sketch, "E102.10.3", {"start": v(14.28, 141.89) * mm, "mid": v(14.34, 142.19) * mm, "end": v(14.21, 142.47) * mm});
            skArc(sketch, "E102.10.4", {"start": v(14.21, 142.47) * mm, "mid": v(13.63, 143.08) * mm, "end": v(13.02, 143.67) * mm});
            skArc(sketch, "E102.10.5", {"start": v(13.02, 143.67) * mm, "mid": v(12.73, 143.8) * mm, "end": v(12.43, 143.73) * mm});
            skLineSegment(sketch, "E102.10.6", {"start": v(12.43, 143.73) * mm, "end": v(8.31, 141.38) * mm});
            skArc(sketch, "E102.10.7", {"start": v(7.79, 141.4) * mm, "mid": v(8.05, 141.31) * mm, "end": v(8.31, 141.38) * mm});
            skLineSegment(sketch, "E102.10.8", {"start": v(7.79, 141.4) * mm, "end": v(7.31, 141.72) * mm});
            skLineSegment(sketch, "E102.11.0", {"start": v(6.8, 141.97) * mm, "end": v(7.31, 141.72) * mm});
            skArc(sketch, "E102.11.1", {"start": v(6.52, 142.42) * mm, "mid": v(6.6, 142.15) * mm, "end": v(6.8, 141.97) * mm});
            skLineSegment(sketch, "E102.11.2", {"start": v(6.5, 147.16) * mm, "end": v(6.52, 142.42) * mm});
            skArc(sketch, "E102.11.3", {"start": v(6.5, 147.16) * mm, "mid": v(6.4, 147.45) * mm, "end": v(6.15, 147.63) * mm});
            skArc(sketch, "E102.11.4", {"start": v(6.15, 147.63) * mm, "mid": v(5.33, 147.87) * mm, "end": v(4.51, 148.07) * mm});
            skArc(sketch, "E102.11.5", {"start": v(4.51, 148.07) * mm, "mid": v(4.2, 148.04) * mm, "end": v(3.97, 147.83) * mm});
            skLineSegment(sketch, "E102.11.6", {"start": v(3.97, 147.83) * mm, "end": v(1.58, 143.74) * mm});
            skArc(sketch, "E102.11.7", {"start": v(1.12, 143.5) * mm, "mid": v(1.39, 143.55) * mm, "end": v(1.58, 143.74) * mm});
            skLineSegment(sketch, "E102.11.8", {"start": v(1.12, 143.5) * mm, "end": v(0.55, 143.53) * mm});
            skSolve(sketch);
        }
        {
            var Q0;
            Q0=qSketchRegion(id+"F6",true);
            extrude(context, id + "F7", {"entities" : qUnion([Q0]), "depth" : 5 * mm});
        }
        {
            var Q0;
            Q0=makeQuery(id+"F7.opExtrude","CAP_FACE",FACE,{"disambiguationData":[OSD([sQuery(id+"F6.wireOp",EDGE,"E81"),sQuery(id+"F6.wireOp",EDGE,"E83")])],"isStart":false});
            var sketch = newSketch(context, id + "F8", { "sketchPlane" : qUnion([Q0])});
            skLineSegment(sketch, "E103.rect.top", {"start": v(45.55, 137.5) * mm, "end": v(-49.45, 137.5) * mm});
            skLineSegment(sketch, "E103.rect.left", {"start": v(50.55, 130) * mm, "end": v(50.55, 132.5) * mm});
            skLineSegment(sketch, "E103.rect.right", {"start": v(-49.45, 122.5) * mm, "end": v(-49.45, 127.5) * mm});
            skPoint(sketch, "E103.rect.middle", {"position": v(0.55, 130) * mm});
            skCircle(sketch, "E104", {"center": v(0.55, 130) * mm, "radius": 1.6 * mm});
            skPoint(sketch, "E105.endSnap0", {"position": v(50.55, 130) * mm});
            skPoint(sketch, "E106.orphan", {"position": v(-49.45, 137.5) * mm});
            skPoint(sketch, "E107.orphan", {"position": v(50.55, 122.5) * mm});
            skLineSegment(sketch, "E108", {"start": v(-49.45, 137.5) * mm, "end": v(50.55, 122.5) * mm, "construction": true});
            skLineSegment(sketch, "E109", {"start": v(0.55, 130) * mm, "end": v(-49.45, 130) * mm, "construction": true});
            skLineSegment(sketch, "E110", {"start": v(-49.45, 137.5) * mm, "end": v(-49.45, 132.5) * mm});
            skLineSegment(sketch, "E111", {"start": v(-49.45, 132.5) * mm, "end": v(-44.45, 132.5) * mm});
            skLineSegment(sketch, "E112", {"start": v(-44.45, 132.5) * mm, "end": v(-44.45, 127.5) * mm});
            skLineSegment(sketch, "E113", {"start": v(-44.45, 127.5) * mm, "end": v(-49.45, 127.5) * mm});
            skLineSegment(sketch, "E114", {"start": v(-49.45, 132.5) * mm, "end": v(-49.45, 127.5) * mm, "construction": true});
            skLineSegment(sketch, "E115", {"start": v(50.55, 127.5) * mm, "end": v(50.55, 130) * mm});
            skLineSegment(sketch, "E116", {"start": v(45.55, 137.5) * mm, "end": v(45.55, 132.5) * mm});
            skLineSegment(sketch, "E117", {"start": v(45.55, 132.5) * mm, "end": v(50.55, 132.5) * mm});
            skLineSegment(sketch, "E118", {"start": v(45.55, 122.5) * mm, "end": v(45.55, 127.5) * mm});
            skLineSegment(sketch, "E119", {"start": v(45.55, 127.5) * mm, "end": v(50.55, 127.5) * mm});
            skPoint(sketch, "E119.endSnap0", {"position": v(50.55, 126.25) * mm});
            skLineSegment(sketch, "E120", {"start": v(50.55, 132.5) * mm, "end": v(50.55, 127.5) * mm, "construction": true});
            skPoint(sketch, "E121.orphan", {"position": v(50.55, 137.5) * mm});
            skCircle(sketch, "E122", {"center": v(353, 0) * mm, "radius": 90 * mm, "construction": true});
            skLineSegment(sketch, "E123.0", {"start": v(263, 0) * mm, "end": v(308, 77.94) * mm, "construction": true});
            skLineSegment(sketch, "E123.1", {"start": v(308, 77.94) * mm, "end": v(398, 77.94) * mm, "construction": true});
            skLineSegment(sketch, "E123.2", {"start": v(398, 77.94) * mm, "end": v(443, 0) * mm, "construction": true});
            skLineSegment(sketch, "E123.3", {"start": v(443, 0) * mm, "end": v(398, -77.94) * mm, "construction": true});
            skLineSegment(sketch, "E123.4", {"start": v(398, -77.94) * mm, "end": v(308, -77.94) * mm, "construction": true});
            skLineSegment(sketch, "E123.5", {"start": v(308, -77.94) * mm, "end": v(263, 0) * mm, "construction": true});
            skLineSegment(sketch, "E124", {"start": v(45.55, 122.5) * mm, "end": v(-49.45, 122.5) * mm});
            skCircle(sketch, "E125", {"center": v(-32.79, 130) * mm, "radius": 1.6 * mm});
            skSolve(sketch);
        }
        {
            var Q0;
            Q0=qSketchRegion(id+"F8",true);
            extrude(context, id + "F9", {"entities" : qUnion([Q0]), "depth" : 5 * mm});
        }
        {
            var Q0;
            Q0=makeQuery(id+"F9.opExtrude","CAP_EDGE",EDGE,{"disambiguationData":[OSD([sQuery(id+"F8.wireOp",EDGE,"E110")])],"isStart":true});
            cPlane(context, id + "F10", {"entities" : qUnion([Q0]), "cplaneType" : CPlaneType.LINE_ANGLE, "offset" : 150 * mm, "angle" : 120 * degree, "width" : 150 * mm, "height" : 150 * mm});
        }
        {
            var Q0;
            Q0=qCreatedBy(id+"F10.planeOp",FACE);
            var sketch = newSketch(context, id + "F11", { "sketchPlane" : qUnion([Q0])});
            skLineSegment(sketch, "E126", {"start": v(53.22, 132.5) * mm, "end": v(53.22, 127.5) * mm});
            skLineSegment(sketch, "E127", {"start": v(53.22, 132.5) * mm, "end": v(48.22, 132.5) * mm});
            skLineSegment(sketch, "E128", {"start": v(48.22, 132.5) * mm, "end": v(48.22, 137.5) * mm});
            skLineSegment(sketch, "E129", {"start": v(48.22, 137.5) * mm, "end": v(-46.78, 137.5) * mm});
            skLineSegment(sketch, "E130", {"start": v(-46.78, 137.5) * mm, "end": v(-46.78, 132.5) * mm});
            skLineSegment(sketch, "E131", {"start": v(-46.78, 132.5) * mm, "end": v(-41.78, 132.5) * mm});
            skLineSegment(sketch, "E132", {"start": v(-41.78, 132.5) * mm, "end": v(-41.78, 127.5) * mm});
            skLineSegment(sketch, "E133", {"start": v(-41.78, 127.5) * mm, "end": v(-46.78, 127.5) * mm});
            skLineSegment(sketch, "E134", {"start": v(-46.78, 127.5) * mm, "end": v(-46.78, 122.5) * mm});
            skLineSegment(sketch, "E135", {"start": v(-46.78, 122.5) * mm, "end": v(48.22, 122.5) * mm});
            skLineSegment(sketch, "E136", {"start": v(48.22, 122.5) * mm, "end": v(48.22, 127.5) * mm});
            skLineSegment(sketch, "E137", {"start": v(48.22, 127.5) * mm, "end": v(53.22, 127.5) * mm});
            skLineSegment(sketch, "E138", {"start": v(53.22, 137.5) * mm, "end": v(-46.78, 122.5) * mm, "construction": true});
            skLineSegment(sketch, "E139", {"start": v(53.22, 130) * mm, "end": v(-46.78, 130) * mm, "construction": true});
            skCircle(sketch, "E140", {"center": v(3.22, 130) * mm, "radius": 1.6 * mm});
            skCircle(sketch, "E141", {"center": v(36.55, 130) * mm, "radius": 1.6 * mm});
            skCircle(sketch, "E142", {"center": v(-26.78, 130) * mm, "radius": 1.6 * mm, "construction": true});
            skSolve(sketch);
        }
        {
            var Q0;
            Q0=makeQuery(id+"F11.imprint","IMPRINT",FACE,{"disambiguationData":[TD([[makeQuery(id+"F11.imprint","IMPRINT",EDGE,{"derivedFrom":sQuery(id+"F11.wireOp",EDGE,"E126")}),-1.0]])]});
            extrude(context, id + "F12", {"entities" : qUnion([Q0]), "depth" : 5 * mm});
        }
        {
            var Q0;
            Q0=makeQuery(id+"F9.opExtrude","CAP_FACE",FACE,{"disambiguationData":[OSD([sQuery(id+"F8.wireOp",EDGE,"E103.rect.top"),sQuery(id+"F8.wireOp",EDGE,"E103.rect.left"),sQuery(id+"F8.wireOp",EDGE,"E103.rect.right"),sQuery(id+"F8.wireOp",EDGE,"E104"),sQuery(id+"F8.wireOp",EDGE,"E110"),sQuery(id+"F8.wireOp",EDGE,"E111"),sQuery(id+"F8.wireOp",EDGE,"E112"),sQuery(id+"F8.wireOp",EDGE,"E113"),sQuery(id+"F8.wireOp",EDGE,"E115"),sQuery(id+"F8.wireOp",EDGE,"E116"),sQuery(id+"F8.wireOp",EDGE,"E117"),sQuery(id+"F8.wireOp",EDGE,"E118"),sQuery(id+"F8.wireOp",EDGE,"E119"),sQuery(id+"F8.wireOp",EDGE,"E124"),sQuery(id+"F8.wireOp",EDGE,"E125")])],"isStart":false});
            cPlane(context, id + "F13", {"entities" : qUnion([Q0]), "cplaneType" : CPlaneType.OFFSET, "offset" : 10 * mm, "width" : 150 * mm, "height" : 150 * mm});
        }
        {
            var Q0;
            Q0=qCreatedBy(id+"F13.planeOp",FACE);
            var sketch = newSketch(context, id + "F14", { "sketchPlane" : qUnion([Q0])});
            skLineSegment(sketch, "E143", {"start": v(-44.45, 132.5) * mm, "end": v(-44.45, 137.5) * mm});
            skLineSegment(sketch, "E144", {"start": v(-44.45, 137.5) * mm, "end": v(40.55, 137.5) * mm});
            skLineSegment(sketch, "E145", {"start": v(40.55, 137.5) * mm, "end": v(40.55, 132.5) * mm});
            skLineSegment(sketch, "E146", {"start": v(40.55, 132.5) * mm, "end": v(45.55, 132.5) * mm});
            skLineSegment(sketch, "E147", {"start": v(45.55, 132.5) * mm, "end": v(45.55, 127.5) * mm});
            skLineSegment(sketch, "E148", {"start": v(45.55, 127.5) * mm, "end": v(40.55, 127.5) * mm});
            skLineSegment(sketch, "E149", {"start": v(40.55, 127.5) * mm, "end": v(40.55, 122.5) * mm});
            skLineSegment(sketch, "E150", {"start": v(40.55, 122.5) * mm, "end": v(-44.45, 122.5) * mm});
            skLineSegment(sketch, "E151", {"start": v(-44.45, 122.5) * mm, "end": v(-44.45, 127.5) * mm});
            skLineSegment(sketch, "E152", {"start": v(-44.45, 127.5) * mm, "end": v(-39.45, 127.5) * mm});
            skLineSegment(sketch, "E153", {"start": v(-39.45, 127.5) * mm, "end": v(-39.45, 132.5) * mm});
            skLineSegment(sketch, "E154", {"start": v(-39.45, 132.5) * mm, "end": v(-44.45, 132.5) * mm});
            skLineSegment(sketch, "E155", {"start": v(-44.45, 137.5) * mm, "end": v(45.55, 122.5) * mm, "construction": true});
            skPoint(sketch, "E156", {"position": v(0.55, 130) * mm});
            skCircle(sketch, "E157", {"center": v(0.55, 130) * mm, "radius": 1.5 * mm});
            skSolve(sketch);
        }
        {
            var Q0;
            Q0=makeQuery(id+"F14.imprint","IMPRINT",FACE,{"disambiguationData":[TD([[makeQuery(id+"F14.imprint","IMPRINT",EDGE,{"derivedFrom":sQuery(id+"F14.wireOp",EDGE,"E143")}),-1.0]])]});
            extrude(context, id + "F15", {"entities" : qUnion([Q0]), "depth" : 5 * mm});
        }
        {
            var Q0;
            Q0=makeQuery(id+"F12.opExtrude","CAP_EDGE",EDGE,{"disambiguationData":[OSD([sQuery(id+"F11.wireOp",EDGE,"E130")])],"isStart":true});
            cPlane(context, id + "F16", {"entities" : qUnion([Q0]), "cplaneType" : CPlaneType.LINE_ANGLE, "offset" : 150 * mm, "angle" : 240 * degree, "width" : 150 * mm, "height" : 150 * mm});
        }
        {
            var Q0;
            Q0=qCreatedBy(id+"F16.planeOp",FACE);
            var sketch = newSketch(context, id + "F17", { "sketchPlane" : qUnion([Q0])});
            skLineSegment(sketch, "E158", {"start": v(-52.67, 132.5) * mm, "end": v(-52.67, 127.5) * mm});
            skLineSegment(sketch, "E159", {"start": v(-52.67, 127.5) * mm, "end": v(-47.67, 127.5) * mm});
            skLineSegment(sketch, "E160", {"start": v(-47.67, 127.5) * mm, "end": v(-47.67, 122.5) * mm});
            skLineSegment(sketch, "E161", {"start": v(-47.67, 122.5) * mm, "end": v(47.33, 122.5) * mm});
            skLineSegment(sketch, "E162", {"start": v(47.33, 122.5) * mm, "end": v(47.33, 127.5) * mm});
            skLineSegment(sketch, "E163", {"start": v(47.33, 127.5) * mm, "end": v(42.33, 127.5) * mm});
            skLineSegment(sketch, "E164", {"start": v(42.33, 127.5) * mm, "end": v(42.33, 132.5) * mm});
            skLineSegment(sketch, "E165", {"start": v(42.33, 132.5) * mm, "end": v(47.33, 132.5) * mm});
            skLineSegment(sketch, "E166", {"start": v(47.33, 132.5) * mm, "end": v(47.33, 137.5) * mm});
            skLineSegment(sketch, "E167", {"start": v(47.33, 137.5) * mm, "end": v(-47.67, 137.5) * mm});
            skLineSegment(sketch, "E168", {"start": v(-47.67, 137.5) * mm, "end": v(-47.67, 132.5) * mm});
            skLineSegment(sketch, "E169", {"start": v(-47.67, 132.5) * mm, "end": v(-52.67, 132.5) * mm});
            skSolve(sketch);
        }
        {
            var Q0;
            Q0=makeQuery(id+"F17.imprint","IMPRINT",FACE,{"disambiguationData":[TD([[makeQuery(id+"F17.imprint","IMPRINT",EDGE,{"derivedFrom":sQuery(id+"F17.wireOp",EDGE,"E158")}),1.0]])]});
            extrude(context, id + "F18", {"entities" : qUnion([Q0]), "oppositeDirection" : true, "depth" : 5 * mm});
        }
        {
            var Q0;
            Q0=makeQuery(id+"F18.opExtrude","CAP_EDGE",EDGE,{"disambiguationData":[OSD([sQuery(id+"F17.wireOp",EDGE,"E166")])],"isStart":true});
            cPlane(context, id + "F19", {"entities" : qUnion([Q0]), "cplaneType" : CPlaneType.LINE_ANGLE, "offset" : 150 * mm, "angle" : 0 * degree, "width" : 150 * mm, "height" : 150 * mm});
        }
        {
            var Q0;
            Q0=qCreatedBy(id+"F19.planeOp",FACE);
            var sketch = newSketch(context, id + "F20", { "sketchPlane" : qUnion([Q0])});
            skLineSegment(sketch, "E170", {"start": v(-49.45, 132.5) * mm, "end": v(-49.45, 127.5) * mm});
            skLineSegment(sketch, "E171", {"start": v(-49.45, 127.5) * mm, "end": v(-44.45, 127.5) * mm});
            skLineSegment(sketch, "E172", {"start": v(-44.45, 127.5) * mm, "end": v(-44.45, 122.5) * mm});
            skLineSegment(sketch, "E173", {"start": v(-44.45, 122.5) * mm, "end": v(50.55, 122.5) * mm});
            skLineSegment(sketch, "E174", {"start": v(50.55, 122.5) * mm, "end": v(50.55, 127.5) * mm});
            skLineSegment(sketch, "E175", {"start": v(50.55, 127.5) * mm, "end": v(45.55, 127.5) * mm});
            skLineSegment(sketch, "E176", {"start": v(45.55, 127.5) * mm, "end": v(45.55, 132.5) * mm});
            skLineSegment(sketch, "E177", {"start": v(45.55, 132.5) * mm, "end": v(50.55, 132.5) * mm});
            skLineSegment(sketch, "E178", {"start": v(50.55, 132.5) * mm, "end": v(50.55, 137.5) * mm});
            skLineSegment(sketch, "E179", {"start": v(50.55, 137.5) * mm, "end": v(-44.45, 137.5) * mm});
            skLineSegment(sketch, "E180", {"start": v(-44.45, 137.5) * mm, "end": v(-44.45, 132.5) * mm});
            skLineSegment(sketch, "E181", {"start": v(-44.45, 132.5) * mm, "end": v(-49.45, 132.5) * mm});
            skLineSegment(sketch, "E182", {"start": v(-49.45, 137.5) * mm, "end": v(50.55, 122.5) * mm, "construction": true});
            skCircle(sketch, "E183", {"center": v(0, 130.08) * mm, "radius": 1.6 * mm});
            skSolve(sketch);
        }
        {
            var Q0;
            Q0=makeQuery(id+"F20.imprint","IMPRINT",FACE,{"disambiguationData":[TD([[makeQuery(id+"F20.imprint","IMPRINT",EDGE,{"derivedFrom":sQuery(id+"F20.wireOp",EDGE,"E170")}),1.0]])]});
            extrude(context, id + "F21", {"entities" : qUnion([Q0]), "oppositeDirection" : true, "depth" : 5 * mm});
        }
        {
            var Q0;
            Q0=makeQuery(id+"F9.opExtrude","CAP_FACE",FACE,{"disambiguationData":[OSD([sQuery(id+"F8.wireOp",EDGE,"E103.rect.top"),sQuery(id+"F8.wireOp",EDGE,"E103.rect.left"),sQuery(id+"F8.wireOp",EDGE,"E103.rect.right"),sQuery(id+"F8.wireOp",EDGE,"E104"),sQuery(id+"F8.wireOp",EDGE,"E110"),sQuery(id+"F8.wireOp",EDGE,"E111"),sQuery(id+"F8.wireOp",EDGE,"E112"),sQuery(id+"F8.wireOp",EDGE,"E113"),sQuery(id+"F8.wireOp",EDGE,"E115"),sQuery(id+"F8.wireOp",EDGE,"E116"),sQuery(id+"F8.wireOp",EDGE,"E117"),sQuery(id+"F8.wireOp",EDGE,"E118"),sQuery(id+"F8.wireOp",EDGE,"E119"),sQuery(id+"F8.wireOp",EDGE,"E124"),sQuery(id+"F8.wireOp",EDGE,"E125")])],"isStart":false});
            var sketch = newSketch(context, id + "F22", { "sketchPlane" : qUnion([Q0])});
            skCircle(sketch, "E184", {"center": v(0.55, 130) * mm, "radius": 1.6 * mm});
            skCircle(sketch, "E185", {"center": v(0.55, 130) * mm, "radius": 7.5 * mm});
            skSolve(sketch);
        }
        {
            var Q0;
            Q0=makeQuery(id+"F22.imprint","IMPRINT",FACE,{"disambiguationData":[TD([[makeQuery(id+"F22.imprint","IMPRINT",EDGE,{"derivedFrom":sQuery(id+"F22.wireOp",EDGE,"E184")}),-1.0]])]});
            extrude(context, id + "F23", {"entities" : qUnion([Q0]), "depth" : 3 * mm});
        }
        {
            var Q0;
            Q0=makeQuery(id+"F3.opExtrude","CAP_FACE",FACE,{"disambiguationData":[OSD([sQuery(id+"F2.wireOp",EDGE,"E29.bottom"),sQuery(id+"F2.wireOp",EDGE,"E30"),sQuery(id+"F2.wireOp",EDGE,"E31"),sQuery(id+"F2.wireOp",EDGE,"E32"),sQuery(id+"F2.wireOp",EDGE,"E33"),sQuery(id+"F2.wireOp",EDGE,"E34"),sQuery(id+"F2.wireOp",EDGE,"E36.filletArc"),sQuery(id+"F2.wireOp",EDGE,"E37.filletArc"),sQuery(id+"F2.wireOp",EDGE,"E38.filletArc"),sQuery(id+"F2.wireOp",EDGE,"E39.filletArc"),sQuery(id+"F2.wireOp",EDGE,"E41"),sQuery(id+"F2.wireOp",EDGE,"E42.top"),sQuery(id+"F2.wireOp",EDGE,"E42.right"),sQuery(id+"F2.wireOp",EDGE,"E43.1.0.0"),sQuery(id+"F2.wireOp",EDGE,"E43.1.0.1"),sQuery(id+"F2.wireOp",EDGE,"E43.1.0.2"),sQuery(id+"F2.wireOp",EDGE,"E43.2.0.0"),sQuery(id+"F2.wireOp",EDGE,"E43.2.0.1"),sQuery(id+"F2.wireOp",EDGE,"E43.2.0.2"),sQuery(id+"F2.wireOp",EDGE,"E43.3.0.0"),sQuery(id+"F2.wireOp",EDGE,"E43.3.0.1"),sQuery(id+"F2.wireOp",EDGE,"E43.3.0.2"),sQuery(id+"F2.wireOp",EDGE,"E43.4.0.0"),sQuery(id+"F2.wireOp",EDGE,"E43.4.0.1"),sQuery(id+"F2.wireOp",EDGE,"E43.4.0.2"),sQuery(id+"F2.wireOp",EDGE,"E43.5.0.0"),sQuery(id+"F2.wireOp",EDGE,"E43.5.0.1"),sQuery(id+"F2.wireOp",EDGE,"E43.5.0.2"),sQuery(id+"F2.wireOp",EDGE,"E43.6.0.0"),sQuery(id+"F2.wireOp",EDGE,"E43.6.0.1"),sQuery(id+"F2.wireOp",EDGE,"E43.6.0.2"),sQuery(id+"F2.wireOp",EDGE,"E43.7.0.0"),sQuery(id+"F2.wireOp",EDGE,"E43.7.0.1"),sQuery(id+"F2.wireOp",EDGE,"E43.7.0.2"),sQuery(id+"F2.wireOp",EDGE,"E43.8.0.0"),sQuery(id+"F2.wireOp",EDGE,"E43.8.0.1"),sQuery(id+"F2.wireOp",EDGE,"E43.8.0.2"),sQuery(id+"F2.wireOp",EDGE,"E43.9.0.0"),sQuery(id+"F2.wireOp",EDGE,"E43.9.0.1"),sQuery(id+"F2.wireOp",EDGE,"E43.9.0.2"),sQuery(id+"F2.wireOp",EDGE,"E43.10.0.0"),sQuery(id+"F2.wireOp",EDGE,"E43.10.0.1"),sQuery(id+"F2.wireOp",EDGE,"E43.10.0.2"),sQuery(id+"F2.wireOp",EDGE,"E43.11.0.0"),sQuery(id+"F2.wireOp",EDGE,"E43.11.0.1"),sQuery(id+"F2.wireOp",EDGE,"E43.11.0.2"),sQuery(id+"F2.wireOp",EDGE,"E44.trimOffspring"),sQuery(id+"F2.wireOp",EDGE,"E45.trimOffspring"),sQuery(id+"F2.wireOp",EDGE,"E46.trimOffspring"),sQuery(id+"F2.wireOp",EDGE,"E47.trimOffspring"),sQuery(id+"F2.wireOp",EDGE,"E48.trimOffspring"),sQuery(id+"F2.wireOp",EDGE,"E49.trimOffspring"),sQuery(id+"F2.wireOp",EDGE,"E50.trimOffspring"),sQuery(id+"F2.wireOp",EDGE,"E51.trimOffspring"),sQuery(id+"F2.wireOp",EDGE,"E52.trimOffspring"),sQuery(id+"F2.wireOp",EDGE,"E53.trimOffspring"),sQuery(id+"F2.wireOp",EDGE,"E54.trimOffspring"),sQuery(id+"F2.wireOp",EDGE,"E55.rect.bottom"),sQuery(id+"F2.wireOp",EDGE,"E55.rect.top"),sQuery(id+"F2.wireOp",EDGE,"E55.rect.left"),sQuery(id+"F2.wireOp",EDGE,"E55.rect.right")])],"isStart":true});
            var sketch = newSketch(context, id + "F24", { "sketchPlane" : qUnion([Q0])});
            skLineSegment(sketch, "E186.left", {"start": v(11.35, 139.76) * mm, "end": v(11.35, 94.5) * mm});
            skLineSegment(sketch, "E186.right", {"start": v(-11.65, 139.74) * mm, "end": v(-11.65, 94.5) * mm});
            skPoint(sketch, "E186.middle", {"position": v(0, 81.55) * mm});
            skLineSegment(sketch, "E187", {"start": v(-0.15, 141.5) * mm, "end": v(0.15, 21.6) * mm, "construction": true});
            skLineSegment(sketch, "E188", {"start": v(-11.65, 118.5) * mm, "end": v(11.35, 118.5) * mm, "construction": true});
            skLineSegment(sketch, "E189", {"start": v(11.35, 118.5) * mm, "end": v(11.35, 139.76) * mm, "construction": true});
            skLineSegment(sketch, "E190", {"start": v(11.35, 118.5) * mm, "end": v(-11.65, 141.5) * mm, "construction": true});
            skPoint(sketch, "E191", {"position": v(-0.15, 130) * mm});
            skLineSegment(sketch, "E192", {"start": v(-11.65, 94.5) * mm, "end": v(11.35, 94.5) * mm});
            skLineSegment(sketch, "E193.0", {"start": v(26.35, 131.83) * mm, "end": v(26.35, 79.5) * mm});
            skLineSegment(sketch, "E193.2", {"start": v(-26.65, 131.67) * mm, "end": v(-26.65, 79.5) * mm});
            skLineSegment(sketch, "E193.3", {"start": v(-26.65, 79.5) * mm, "end": v(26.35, 79.5) * mm});
            skLineSegment(sketch, "E194", {"start": v(-58.31, 54.36) * mm, "end": v(-31.34, 124.03) * mm, "construction": true});
            skLineSegment(sketch, "E195", {"start": v(31.19, 123.99) * mm, "end": v(58.01, 54.36) * mm, "construction": true});
            skPoint(sketch, "E196.orphan", {"position": v(0, 204.96) * mm});
            skPoint(sketch, "E197.visualSharp", {"position": v(-25.15, 140) * mm});
            skArc(sketch, "E197.filletArc", {"start": v(-11.65, 139.74) * mm, "mid": v(-19.86, 137.02) * mm, "end": v(-26.65, 131.67) * mm});
            skPoint(sketch, "E198.visualSharp", {"position": v(25.02, 140) * mm});
            skArc(sketch, "E198.filletArc", {"start": v(26.35, 131.83) * mm, "mid": v(19.54, 137.1) * mm, "end": v(11.35, 139.76) * mm});
            skPoint(sketch, "E199.orphan", {"position": v(11.35, 141.5) * mm});
            skSolve(sketch);
        }
        {
            var Q0;
            Q0 = qSketchRegion(id + "F24", true);
            extrude(context, id + "F25", {"entities" : qUnion([Q0]), "depth" : 5 * mm});
        }
        {
            var Q0;
            Q0=makeQuery(id+"F12.opExtrude","CAP_FACE",FACE,{"disambiguationData":[OSD([sQuery(id+"F11.wireOp",EDGE,"E126"),sQuery(id+"F11.wireOp",EDGE,"E127"),sQuery(id+"F11.wireOp",EDGE,"E128"),sQuery(id+"F11.wireOp",EDGE,"E129"),sQuery(id+"F11.wireOp",EDGE,"E130"),sQuery(id+"F11.wireOp",EDGE,"E131"),sQuery(id+"F11.wireOp",EDGE,"E132"),sQuery(id+"F11.wireOp",EDGE,"E133"),sQuery(id+"F11.wireOp",EDGE,"E134"),sQuery(id+"F11.wireOp",EDGE,"E135"),sQuery(id+"F11.wireOp",EDGE,"E136"),sQuery(id+"F11.wireOp",EDGE,"E137"),sQuery(id+"F11.wireOp",EDGE,"E140"),sQuery(id+"F11.wireOp",EDGE,"E141")])],"isStart":true});
            var sketch = newSketch(context, id + "F26", { "sketchPlane" : qUnion([Q0])});
            skArc(sketch, "E200", {"start": v(0.67, 144.49) * mm, "mid": v(-7.1, 115.51) * mm, "end": v(0.69, 144.48) * mm});
            skCircle(sketch, "E201", {"center": v(-36.55, 130) * mm, "radius": 16.5 * mm, "construction": true});
            skLineSegment(sketch, "E202", {"start": v(-36.55, 130) * mm, "end": v(-3.22, 130) * mm, "construction": true});
            skLineSegment(sketch, "E203", {"start": v(-19.88, 108.94) * mm, "end": v(-19.88, 151.06) * mm, "construction": true});
            skPoint(sketch, "E204", {"position": v(-19.88, 130) * mm});
            skLineSegment(sketch, "E205", {"start": v(-3.22, 130) * mm, "end": v(-3.22, 148) * mm, "construction": true});
            skCircle(sketch, "E206", {"center": v(-3.22, 130) * mm, "radius": 18 * mm, "construction": true});
            skLineSegment(sketch, "E207", {"start": v(-3.22, 130) * mm, "end": v(0.07, 147.7) * mm, "construction": true});
            skLineSegment(sketch, "E208", {"start": v(-3.22, 130) * mm, "end": v(-2.74, 148) * mm, "construction": true});
            skLineSegment(sketch, "E209", {"start": v(-3.22, 130) * mm, "end": v(-2.27, 147.98) * mm, "construction": true});
            skLineSegment(sketch, "E210", {"start": v(-3.22, 130) * mm, "end": v(-1.33, 147.9) * mm, "construction": true});
            skLineSegment(sketch, "E211", {"start": v(-3.22, 130) * mm, "end": v(-1.8, 147.94) * mm, "construction": true});
            skLineSegment(sketch, "E212", {"start": v(-3.22, 130) * mm, "end": v(-0.87, 147.85) * mm, "construction": true});
            skLineSegment(sketch, "E213", {"start": v(-3.22, 130) * mm, "end": v(-0.4, 147.78) * mm, "construction": true});
            skLineSegment(sketch, "E214", {"start": v(-3.22, 130) * mm, "end": v(0.53, 147.6) * mm, "construction": true});
            skLineSegment(sketch, "E215", {"start": v(-3.22, 130) * mm, "end": v(0.99, 147.5) * mm, "construction": true});
            skLineSegment(sketch, "E216", {"start": v(-3.22, 130) * mm, "end": v(1.44, 147.39) * mm, "construction": true});
            skLineSegment(sketch, "E217", {"start": v(-2.26, 145.8) * mm, "end": v(-1.99, 147.06) * mm});
            skLineSegment(sketch, "E218", {"start": v(-0.05, 145.5) * mm, "end": v(0.02, 146.8) * mm});
            skArc(sketch, "E219", {"start": v(-0.88, 147.85) * mm, "mid": v(-0.87, 147.85) * mm, "end": v(-0.85, 147.84) * mm});
            skArc(sketch, "E220.trimOffspring", {"start": v(-3.23, 145) * mm, "mid": v(-3.2, 115) * mm, "end": v(-3.22, 145) * mm});
            skPoint(sketch, "E221.visualSharp", {"position": v(-2.43, 144.98) * mm});
            skArc(sketch, "E221.filletArc", {"start": v(-3.23, 145) * mm, "mid": v(-2.6, 145.22) * mm, "end": v(-2.26, 145.8) * mm});
            skPoint(sketch, "E222.visualSharp", {"position": v(-1.8, 147.94) * mm});
            skArc(sketch, "E222.filletArc", {"start": v(-0.88, 147.85) * mm, "mid": v(-1.59, 147.67) * mm, "end": v(-1.99, 147.06) * mm});
            skPoint(sketch, "E223.visualSharp", {"position": v(0.07, 147.7) * mm});
            skArc(sketch, "E223.filletArc", {"start": v(0.02, 146.8) * mm, "mid": v(-0.21, 147.5) * mm, "end": v(-0.85, 147.84) * mm});
            skPoint(sketch, "E224.visualSharp", {"position": v(-0.1, 144.67) * mm});
            skArc(sketch, "E224.filletArc", {"start": v(-0.05, 145.5) * mm, "mid": v(0.14, 144.86) * mm, "end": v(0.69, 144.48) * mm});
            skLineSegment(sketch, "E225.1.0", {"start": v(-6.38, 145.5) * mm, "end": v(-6.45, 146.8) * mm});
            skLineSegment(sketch, "E225.1.1", {"start": v(-4.17, 145.8) * mm, "end": v(-4.44, 147.06) * mm});
            skArc(sketch, "E225.1.2", {"start": v(-7.12, 144.48) * mm, "mid": v(0.68, 115.51) * mm, "end": v(-7.1, 144.49) * mm});
            skArc(sketch, "E225.1.3", {"start": v(-3.22, 145) * mm, "mid": v(-3.23, 115) * mm, "end": v(-3.2, 145) * mm});
            skArc(sketch, "E225.1.4", {"start": v(-5.58, 147.84) * mm, "mid": v(-6.22, 147.5) * mm, "end": v(-6.45, 146.8) * mm});
            skArc(sketch, "E225.1.5", {"start": v(-7.12, 144.48) * mm, "mid": v(-6.57, 144.86) * mm, "end": v(-6.38, 145.5) * mm});
            skArc(sketch, "E225.1.6", {"start": v(-5.58, 147.84) * mm, "mid": v(-5.56, 147.85) * mm, "end": v(-5.55, 147.85) * mm});
            skArc(sketch, "E225.1.7", {"start": v(-4.17, 145.8) * mm, "mid": v(-3.82, 145.22) * mm, "end": v(-3.2, 145) * mm});
            skArc(sketch, "E225.1.8", {"start": v(-4.44, 147.06) * mm, "mid": v(-4.84, 147.67) * mm, "end": v(-5.55, 147.85) * mm});
            skLineSegment(sketch, "E225.2.0", {"start": v(-10.28, 144.16) * mm, "end": v(-10.69, 145.4) * mm});
            skLineSegment(sketch, "E225.2.1", {"start": v(-8.23, 145) * mm, "end": v(-8.82, 146.16) * mm});
            skArc(sketch, "E225.2.2", {"start": v(-10.73, 142.98) * mm, "mid": v(4.3, 117.01) * mm, "end": v(-10.72, 143) * mm});
            skArc(sketch, "E225.2.3", {"start": v(-7.1, 144.49) * mm, "mid": v(0.66, 115.5) * mm, "end": v(-7.08, 144.5) * mm});
            skArc(sketch, "E225.2.4", {"start": v(-10.12, 146.62) * mm, "mid": v(-10.64, 146.12) * mm, "end": v(-10.69, 145.4) * mm});
            skArc(sketch, "E225.2.5", {"start": v(-10.73, 142.98) * mm, "mid": v(-10.3, 143.49) * mm, "end": v(-10.28, 144.16) * mm});
            skArc(sketch, "E225.2.6", {"start": v(-10.12, 146.62) * mm, "mid": v(-10.1, 146.63) * mm, "end": v(-10.09, 146.64) * mm});
            skArc(sketch, "E225.2.7", {"start": v(-8.23, 145) * mm, "mid": v(-7.74, 144.55) * mm, "end": v(-7.08, 144.5) * mm});
            skArc(sketch, "E225.2.8", {"start": v(-8.82, 146.16) * mm, "mid": v(-9.36, 146.65) * mm, "end": v(-10.09, 146.64) * mm});
            skLineSegment(sketch, "E225.3.0", {"start": v(-13.7, 141.84) * mm, "end": v(-14.41, 142.93) * mm});
            skLineSegment(sketch, "E225.3.1", {"start": v(-11.94, 143.2) * mm, "end": v(-12.8, 144.16) * mm});
            skArc(sketch, "E225.3.2", {"start": v(-13.84, 140.6) * mm, "mid": v(7.4, 119.4) * mm, "end": v(-13.82, 140.6) * mm});
            skArc(sketch, "E225.3.3", {"start": v(-10.72, 143) * mm, "mid": v(4.28, 117) * mm, "end": v(-10.7, 143) * mm});
            skArc(sketch, "E225.3.4", {"start": v(-14.19, 144.27) * mm, "mid": v(-14.56, 143.65) * mm, "end": v(-14.41, 142.93) * mm});
            skArc(sketch, "E225.3.5", {"start": v(-13.84, 140.6) * mm, "mid": v(-13.55, 141.2) * mm, "end": v(-13.7, 141.84) * mm});
            skArc(sketch, "E225.3.6", {"start": v(-14.19, 144.27) * mm, "mid": v(-14.17, 144.28) * mm, "end": v(-14.16, 144.29) * mm});
            skArc(sketch, "E225.3.7", {"start": v(-11.94, 143.2) * mm, "mid": v(-11.35, 142.88) * mm, "end": v(-10.7, 143) * mm});
            skArc(sketch, "E225.3.8", {"start": v(-12.8, 144.16) * mm, "mid": v(-13.46, 144.5) * mm, "end": v(-14.16, 144.29) * mm});
            skLineSegment(sketch, "E225.4.0", {"start": v(-16.41, 138.73) * mm, "end": v(-17.38, 139.6) * mm});
            skLineSegment(sketch, "E225.4.1", {"start": v(-15.06, 140.5) * mm, "end": v(-16.15, 141.2) * mm});
            skArc(sketch, "E225.4.2", {"start": v(-16.22, 137.48) * mm, "mid": v(9.78, 122.5) * mm, "end": v(-16.2, 137.5) * mm});
            skArc(sketch, "E225.4.3", {"start": v(-13.82, 140.6) * mm, "mid": v(7.38, 119.39) * mm, "end": v(-13.8, 140.62) * mm});
            skArc(sketch, "E225.4.4", {"start": v(-17.5, 140.95) * mm, "mid": v(-17.7, 140.24) * mm, "end": v(-17.38, 139.6) * mm});
            skArc(sketch, "E225.4.5", {"start": v(-16.22, 137.48) * mm, "mid": v(-16.1, 138.14) * mm, "end": v(-16.41, 138.73) * mm});
            skArc(sketch, "E225.4.6", {"start": v(-17.5, 140.95) * mm, "mid": v(-17.5, 140.96) * mm, "end": v(-17.49, 140.97) * mm});
            skArc(sketch, "E225.4.7", {"start": v(-15.06, 140.5) * mm, "mid": v(-14.41, 140.33) * mm, "end": v(-13.8, 140.62) * mm});
            skArc(sketch, "E225.4.8", {"start": v(-16.15, 141.2) * mm, "mid": v(-16.86, 141.35) * mm, "end": v(-17.49, 140.97) * mm});
            skLineSegment(sketch, "E225.5.0", {"start": v(-18.22, 135.01) * mm, "end": v(-19.38, 135.6) * mm});
            skLineSegment(sketch, "E225.5.1", {"start": v(-17.37, 137.07) * mm, "end": v(-18.6, 137.47) * mm});
            skArc(sketch, "E225.5.2", {"start": v(-17.7, 133.86) * mm, "mid": v(11.28, 126.13) * mm, "end": v(-17.7, 133.88) * mm});
            skArc(sketch, "E225.5.3", {"start": v(-16.2, 137.5) * mm, "mid": v(9.77, 122.5) * mm, "end": v(-16.2, 137.52) * mm});
            skArc(sketch, "E225.5.4", {"start": v(-19.85, 136.87) * mm, "mid": v(-19.86, 136.14) * mm, "end": v(-19.38, 135.6) * mm});
            skArc(sketch, "E225.5.5", {"start": v(-17.7, 133.86) * mm, "mid": v(-17.76, 134.53) * mm, "end": v(-18.22, 135.01) * mm});
            skArc(sketch, "E225.5.6", {"start": v(-19.85, 136.87) * mm, "mid": v(-19.84, 136.89) * mm, "end": v(-19.84, 136.9) * mm});
            skArc(sketch, "E225.5.7", {"start": v(-17.37, 137.07) * mm, "mid": v(-16.7, 137.08) * mm, "end": v(-16.2, 137.52) * mm});
            skArc(sketch, "E225.5.8", {"start": v(-18.6, 137.47) * mm, "mid": v(-19.33, 137.43) * mm, "end": v(-19.84, 136.9) * mm});
            skLineSegment(sketch, "E225.6.0", {"start": v(-19, 130.96) * mm, "end": v(-20.28, 131.23) * mm});
            skLineSegment(sketch, "E225.6.1", {"start": v(-18.72, 133.16) * mm, "end": v(-20.01, 133.23) * mm});
            skArc(sketch, "E225.6.2", {"start": v(-18.22, 129.98) * mm, "mid": v(11.78, 130) * mm, "end": v(-18.22, 130) * mm});
            skArc(sketch, "E225.6.3", {"start": v(-17.7, 133.88) * mm, "mid": v(11.27, 126.1) * mm, "end": v(-17.7, 133.9) * mm});
            skArc(sketch, "E225.6.4", {"start": v(-21.06, 132.33) * mm, "mid": v(-20.89, 131.63) * mm, "end": v(-20.28, 131.23) * mm});
            skArc(sketch, "E225.6.5", {"start": v(-18.22, 129.98) * mm, "mid": v(-18.44, 130.6) * mm, "end": v(-19, 130.96) * mm});
            skArc(sketch, "E225.6.6", {"start": v(-21.06, 132.33) * mm, "mid": v(-21.06, 132.35) * mm, "end": v(-21.06, 132.37) * mm});
            skArc(sketch, "E225.6.7", {"start": v(-18.72, 133.16) * mm, "mid": v(-18.08, 133.35) * mm, "end": v(-17.7, 133.9) * mm});
            skArc(sketch, "E225.6.8", {"start": v(-20.01, 133.23) * mm, "mid": v(-20.7, 133) * mm, "end": v(-21.06, 132.37) * mm});
            skLineSegment(sketch, "E225.7.0", {"start": v(-18.72, 126.84) * mm, "end": v(-20.01, 126.77) * mm});
            skLineSegment(sketch, "E225.7.1", {"start": v(-19, 129.04) * mm, "end": v(-20.28, 128.77) * mm});
            skArc(sketch, "E225.7.2", {"start": v(-17.7, 126.1) * mm, "mid": v(11.27, 133.9) * mm, "end": v(-17.7, 126.12) * mm});
            skArc(sketch, "E225.7.3", {"start": v(-18.22, 130) * mm, "mid": v(11.78, 130) * mm, "end": v(-18.22, 130.02) * mm});
            skArc(sketch, "E225.7.4", {"start": v(-21.06, 127.63) * mm, "mid": v(-20.7, 127) * mm, "end": v(-20.01, 126.77) * mm});
            skArc(sketch, "E225.7.5", {"start": v(-17.7, 126.1) * mm, "mid": v(-18.08, 126.65) * mm, "end": v(-18.72, 126.84) * mm});
            skArc(sketch, "E225.7.6", {"start": v(-21.06, 127.63) * mm, "mid": v(-21.06, 127.65) * mm, "end": v(-21.06, 127.67) * mm});
            skArc(sketch, "E225.7.7", {"start": v(-19, 129.04) * mm, "mid": v(-18.44, 129.4) * mm, "end": v(-18.22, 130.02) * mm});
            skArc(sketch, "E225.7.8", {"start": v(-20.28, 128.77) * mm, "mid": v(-20.89, 128.37) * mm, "end": v(-21.06, 127.67) * mm});
            skLineSegment(sketch, "E225.8.0", {"start": v(-17.37, 122.93) * mm, "end": v(-18.6, 122.53) * mm});
            skLineSegment(sketch, "E225.8.1", {"start": v(-18.22, 124.99) * mm, "end": v(-19.38, 124.4) * mm});
            skArc(sketch, "E225.8.2", {"start": v(-16.2, 122.48) * mm, "mid": v(9.77, 137.5) * mm, "end": v(-16.2, 122.5) * mm});
            skArc(sketch, "E225.8.3", {"start": v(-17.7, 126.12) * mm, "mid": v(11.28, 133.87) * mm, "end": v(-17.7, 126.14) * mm});
            skArc(sketch, "E225.8.4", {"start": v(-19.84, 123.1) * mm, "mid": v(-19.33, 122.57) * mm, "end": v(-18.6, 122.53) * mm});
            skArc(sketch, "E225.8.5", {"start": v(-16.2, 122.48) * mm, "mid": v(-16.7, 122.92) * mm, "end": v(-17.37, 122.93) * mm});
            skArc(sketch, "E225.8.6", {"start": v(-19.84, 123.1) * mm, "mid": v(-19.84, 123.11) * mm, "end": v(-19.85, 123.13) * mm});
            skArc(sketch, "E225.8.7", {"start": v(-18.22, 124.99) * mm, "mid": v(-17.76, 125.47) * mm, "end": v(-17.7, 126.14) * mm});
            skArc(sketch, "E225.8.8", {"start": v(-19.38, 124.4) * mm, "mid": v(-19.86, 123.86) * mm, "end": v(-19.85, 123.13) * mm});
            skLineSegment(sketch, "E225.9.0", {"start": v(-15.06, 119.5) * mm, "end": v(-16.15, 118.8) * mm});
            skLineSegment(sketch, "E225.9.1", {"start": v(-16.41, 121.27) * mm, "end": v(-17.38, 120.4) * mm});
            skArc(sketch, "E225.9.2", {"start": v(-13.8, 119.38) * mm, "mid": v(7.38, 140.61) * mm, "end": v(-13.82, 119.4) * mm});
            skArc(sketch, "E225.9.3", {"start": v(-16.2, 122.5) * mm, "mid": v(9.78, 137.5) * mm, "end": v(-16.22, 122.52) * mm});
            skArc(sketch, "E225.9.4", {"start": v(-17.49, 119.03) * mm, "mid": v(-16.86, 118.65) * mm, "end": v(-16.15, 118.8) * mm});
            skArc(sketch, "E225.9.5", {"start": v(-13.8, 119.38) * mm, "mid": v(-14.41, 119.67) * mm, "end": v(-15.06, 119.5) * mm});
            skArc(sketch, "E225.9.6", {"start": v(-17.49, 119.03) * mm, "mid": v(-17.5, 119.04) * mm, "end": v(-17.5, 119.05) * mm});
            skArc(sketch, "E225.9.7", {"start": v(-16.41, 121.27) * mm, "mid": v(-16.1, 121.86) * mm, "end": v(-16.22, 122.52) * mm});
            skArc(sketch, "E225.9.8", {"start": v(-17.38, 120.4) * mm, "mid": v(-17.7, 119.76) * mm, "end": v(-17.5, 119.05) * mm});
            skLineSegment(sketch, "E225.10.0", {"start": v(-11.94, 116.8) * mm, "end": v(-12.8, 115.84) * mm});
            skLineSegment(sketch, "E225.10.1", {"start": v(-13.7, 118.16) * mm, "end": v(-14.41, 117.07) * mm});
            skArc(sketch, "E225.10.2", {"start": v(-10.7, 117) * mm, "mid": v(4.28, 143) * mm, "end": v(-10.72, 117) * mm});
            skArc(sketch, "E225.10.3", {"start": v(-13.82, 119.4) * mm, "mid": v(7.4, 140.6) * mm, "end": v(-13.84, 119.4) * mm});
            skArc(sketch, "E225.10.4", {"start": v(-14.16, 115.71) * mm, "mid": v(-13.46, 115.5) * mm, "end": v(-12.8, 115.84) * mm});
            skArc(sketch, "E225.10.5", {"start": v(-10.7, 117) * mm, "mid": v(-11.35, 117.12) * mm, "end": v(-11.94, 116.8) * mm});
            skArc(sketch, "E225.10.6", {"start": v(-14.16, 115.71) * mm, "mid": v(-14.17, 115.72) * mm, "end": v(-14.19, 115.73) * mm});
            skArc(sketch, "E225.10.7", {"start": v(-13.7, 118.16) * mm, "mid": v(-13.55, 118.8) * mm, "end": v(-13.84, 119.4) * mm});
            skArc(sketch, "E225.10.8", {"start": v(-14.41, 117.07) * mm, "mid": v(-14.56, 116.35) * mm, "end": v(-14.19, 115.73) * mm});
            skLineSegment(sketch, "E225.11.0", {"start": v(-8.23, 115) * mm, "end": v(-8.82, 113.84) * mm});
            skLineSegment(sketch, "E225.11.1", {"start": v(-10.28, 115.84) * mm, "end": v(-10.69, 114.6) * mm});
            skArc(sketch, "E225.11.2", {"start": v(-7.08, 115.5) * mm, "mid": v(0.66, 144.5) * mm, "end": v(-7.1, 115.51) * mm});
            skArc(sketch, "E225.11.3", {"start": v(-10.72, 117) * mm, "mid": v(4.3, 142.99) * mm, "end": v(-10.73, 117.02) * mm});
            skArc(sketch, "E225.11.4", {"start": v(-10.09, 113.36) * mm, "mid": v(-9.36, 113.35) * mm, "end": v(-8.82, 113.84) * mm});
            skArc(sketch, "E225.11.5", {"start": v(-7.08, 115.5) * mm, "mid": v(-7.74, 115.45) * mm, "end": v(-8.23, 115) * mm});
            skArc(sketch, "E225.11.6", {"start": v(-10.09, 113.36) * mm, "mid": v(-10.1, 113.37) * mm, "end": v(-10.12, 113.38) * mm});
            skArc(sketch, "E225.11.7", {"start": v(-10.28, 115.84) * mm, "mid": v(-10.3, 116.51) * mm, "end": v(-10.73, 117.02) * mm});
            skArc(sketch, "E225.11.8", {"start": v(-10.69, 114.6) * mm, "mid": v(-10.64, 113.88) * mm, "end": v(-10.12, 113.38) * mm});
            skLineSegment(sketch, "E225.12.0", {"start": v(-4.17, 114.2) * mm, "end": v(-4.44, 112.94) * mm});
            skLineSegment(sketch, "E225.12.1", {"start": v(-6.38, 114.5) * mm, "end": v(-6.45, 113.2) * mm});
            skArc(sketch, "E225.12.2", {"start": v(-3.2, 115) * mm, "mid": v(-3.23, 145) * mm, "end": v(-3.22, 115) * mm});
            skArc(sketch, "E225.12.3", {"start": v(-7.1, 115.51) * mm, "mid": v(0.68, 144.49) * mm, "end": v(-7.12, 115.52) * mm});
            skArc(sketch, "E225.12.4", {"start": v(-5.55, 112.15) * mm, "mid": v(-4.84, 112.33) * mm, "end": v(-4.44, 112.94) * mm});
            skArc(sketch, "E225.12.5", {"start": v(-3.2, 115) * mm, "mid": v(-3.82, 114.78) * mm, "end": v(-4.17, 114.2) * mm});
            skArc(sketch, "E225.12.6", {"start": v(-5.55, 112.15) * mm, "mid": v(-5.56, 112.15) * mm, "end": v(-5.58, 112.16) * mm});
            skArc(sketch, "E225.12.7", {"start": v(-6.38, 114.5) * mm, "mid": v(-6.57, 115.14) * mm, "end": v(-7.12, 115.52) * mm});
            skArc(sketch, "E225.12.8", {"start": v(-6.45, 113.2) * mm, "mid": v(-6.22, 112.5) * mm, "end": v(-5.58, 112.16) * mm});
            skLineSegment(sketch, "E225.13.0", {"start": v(-0.05, 114.5) * mm, "end": v(0.02, 113.2) * mm});
            skLineSegment(sketch, "E225.13.1", {"start": v(-2.26, 114.2) * mm, "end": v(-1.99, 112.94) * mm});
            skArc(sketch, "E225.13.2", {"start": v(0.69, 115.52) * mm, "mid": v(-7.1, 144.49) * mm, "end": v(0.67, 115.51) * mm});
            skArc(sketch, "E225.13.3", {"start": v(-3.22, 115) * mm, "mid": v(-3.2, 145) * mm, "end": v(-3.23, 115) * mm});
            skArc(sketch, "E225.13.4", {"start": v(-0.85, 112.16) * mm, "mid": v(-0.21, 112.5) * mm, "end": v(0.02, 113.2) * mm});
            skArc(sketch, "E225.13.5", {"start": v(0.69, 115.52) * mm, "mid": v(0.14, 115.14) * mm, "end": v(-0.05, 114.5) * mm});
            skArc(sketch, "E225.13.6", {"start": v(-0.85, 112.16) * mm, "mid": v(-0.87, 112.15) * mm, "end": v(-0.88, 112.15) * mm});
            skArc(sketch, "E225.13.7", {"start": v(-2.26, 114.2) * mm, "mid": v(-2.6, 114.78) * mm, "end": v(-3.23, 115) * mm});
            skArc(sketch, "E225.13.8", {"start": v(-1.99, 112.94) * mm, "mid": v(-1.59, 112.33) * mm, "end": v(-0.88, 112.15) * mm});
            skLineSegment(sketch, "E225.14.0", {"start": v(3.85, 115.84) * mm, "end": v(4.25, 114.6) * mm});
            skLineSegment(sketch, "E225.14.1", {"start": v(1.8, 115) * mm, "end": v(2.39, 113.84) * mm});
            skArc(sketch, "E225.14.2", {"start": v(4.3, 117.02) * mm, "mid": v(-10.72, 142.99) * mm, "end": v(4.28, 117) * mm});
            skArc(sketch, "E225.14.3", {"start": v(0.67, 115.51) * mm, "mid": v(-7.09, 144.5) * mm, "end": v(0.65, 115.5) * mm});
            skArc(sketch, "E225.14.4", {"start": v(3.69, 113.38) * mm, "mid": v(4.21, 113.88) * mm, "end": v(4.25, 114.6) * mm});
            skArc(sketch, "E225.14.5", {"start": v(4.3, 117.02) * mm, "mid": v(3.87, 116.51) * mm, "end": v(3.85, 115.84) * mm});
            skArc(sketch, "E225.14.6", {"start": v(3.69, 113.38) * mm, "mid": v(3.67, 113.37) * mm, "end": v(3.66, 113.36) * mm});
            skArc(sketch, "E225.14.7", {"start": v(1.8, 115) * mm, "mid": v(1.31, 115.45) * mm, "end": v(0.65, 115.5) * mm});
            skArc(sketch, "E225.14.8", {"start": v(2.39, 113.84) * mm, "mid": v(2.93, 113.35) * mm, "end": v(3.66, 113.36) * mm});
            skLineSegment(sketch, "E225.15.0", {"start": v(7.28, 118.16) * mm, "end": v(7.98, 117.07) * mm});
            skLineSegment(sketch, "E225.15.1", {"start": v(5.51, 116.8) * mm, "end": v(6.38, 115.84) * mm});
            skArc(sketch, "E225.15.2", {"start": v(7.4, 119.4) * mm, "mid": v(-13.83, 140.6) * mm, "end": v(7.4, 119.4) * mm});
            skArc(sketch, "E225.15.3", {"start": v(4.28, 117) * mm, "mid": v(-10.7, 143) * mm, "end": v(4.27, 117) * mm});
            skArc(sketch, "E225.15.4", {"start": v(7.76, 115.73) * mm, "mid": v(8.13, 116.35) * mm, "end": v(7.98, 117.07) * mm});
            skArc(sketch, "E225.15.5", {"start": v(7.4, 119.4) * mm, "mid": v(7.12, 118.8) * mm, "end": v(7.28, 118.16) * mm});
            skArc(sketch, "E225.15.6", {"start": v(7.76, 115.73) * mm, "mid": v(7.74, 115.72) * mm, "end": v(7.73, 115.71) * mm});
            skArc(sketch, "E225.15.7", {"start": v(5.51, 116.8) * mm, "mid": v(4.92, 117.12) * mm, "end": v(4.27, 117) * mm});
            skArc(sketch, "E225.15.8", {"start": v(6.38, 115.84) * mm, "mid": v(7.03, 115.5) * mm, "end": v(7.73, 115.71) * mm});
            skLineSegment(sketch, "E225.16.0", {"start": v(9.98, 121.27) * mm, "end": v(10.95, 120.4) * mm});
            skLineSegment(sketch, "E225.16.1", {"start": v(8.63, 119.5) * mm, "end": v(9.72, 118.8) * mm});
            skArc(sketch, "E225.16.2", {"start": v(9.79, 122.52) * mm, "mid": v(-16.21, 137.5) * mm, "end": v(9.78, 122.5) * mm});
            skArc(sketch, "E225.16.3", {"start": v(7.4, 119.4) * mm, "mid": v(-13.81, 140.61) * mm, "end": v(7.38, 119.38) * mm});
            skArc(sketch, "E225.16.4", {"start": v(11.07, 119.05) * mm, "mid": v(11.28, 119.76) * mm, "end": v(10.95, 120.4) * mm});
            skArc(sketch, "E225.16.5", {"start": v(9.79, 122.52) * mm, "mid": v(9.66, 121.86) * mm, "end": v(9.98, 121.27) * mm});
            skArc(sketch, "E225.16.6", {"start": v(11.07, 119.05) * mm, "mid": v(11.07, 119.04) * mm, "end": v(11.06, 119.03) * mm});
            skArc(sketch, "E225.16.7", {"start": v(8.63, 119.5) * mm, "mid": v(7.98, 119.67) * mm, "end": v(7.38, 119.38) * mm});
            skArc(sketch, "E225.16.8", {"start": v(9.72, 118.8) * mm, "mid": v(10.43, 118.65) * mm, "end": v(11.06, 119.03) * mm});
            skLineSegment(sketch, "E225.17.0", {"start": v(11.8, 124.99) * mm, "end": v(12.95, 124.4) * mm});
            skLineSegment(sketch, "E225.17.1", {"start": v(10.94, 122.93) * mm, "end": v(12.18, 122.53) * mm});
            skArc(sketch, "E225.17.2", {"start": v(11.28, 126.14) * mm, "mid": v(-17.7, 133.87) * mm, "end": v(11.27, 126.12) * mm});
            skArc(sketch, "E225.17.3", {"start": v(9.78, 122.5) * mm, "mid": v(-16.2, 137.5) * mm, "end": v(9.77, 122.48) * mm});
            skArc(sketch, "E225.17.4", {"start": v(13.42, 123.13) * mm, "mid": v(13.43, 123.86) * mm, "end": v(12.95, 124.4) * mm});
            skArc(sketch, "E225.17.5", {"start": v(11.28, 126.14) * mm, "mid": v(11.33, 125.47) * mm, "end": v(11.8, 124.99) * mm});
            skArc(sketch, "E225.17.6", {"start": v(13.42, 123.13) * mm, "mid": v(13.41, 123.11) * mm, "end": v(13.4, 123.1) * mm});
            skArc(sketch, "E225.17.7", {"start": v(10.94, 122.93) * mm, "mid": v(10.27, 122.92) * mm, "end": v(9.77, 122.48) * mm});
            skArc(sketch, "E225.17.8", {"start": v(12.18, 122.53) * mm, "mid": v(12.9, 122.57) * mm, "end": v(13.4, 123.1) * mm});
            skLineSegment(sketch, "E225.18.0", {"start": v(12.58, 129.04) * mm, "end": v(13.85, 128.77) * mm});
            skLineSegment(sketch, "E225.18.1", {"start": v(12.29, 126.84) * mm, "end": v(13.58, 126.77) * mm});
            skArc(sketch, "E225.18.2", {"start": v(11.78, 130.02) * mm, "mid": v(-18.22, 130) * mm, "end": v(11.78, 130) * mm});
            skArc(sketch, "E225.18.3", {"start": v(11.27, 126.12) * mm, "mid": v(-17.7, 133.9) * mm, "end": v(11.27, 126.1) * mm});
            skArc(sketch, "E225.18.4", {"start": v(14.63, 127.67) * mm, "mid": v(14.46, 128.37) * mm, "end": v(13.85, 128.77) * mm});
            skArc(sketch, "E225.18.5", {"start": v(11.78, 130.02) * mm, "mid": v(12, 129.4) * mm, "end": v(12.58, 129.04) * mm});
            skArc(sketch, "E225.18.6", {"start": v(14.63, 127.67) * mm, "mid": v(14.63, 127.65) * mm, "end": v(14.63, 127.63) * mm});
            skArc(sketch, "E225.18.7", {"start": v(12.29, 126.84) * mm, "mid": v(11.65, 126.65) * mm, "end": v(11.27, 126.1) * mm});
            skArc(sketch, "E225.18.8", {"start": v(13.58, 126.77) * mm, "mid": v(14.28, 127) * mm, "end": v(14.63, 127.63) * mm});
            skLineSegment(sketch, "E225.19.0", {"start": v(12.29, 133.16) * mm, "end": v(13.58, 133.23) * mm});
            skLineSegment(sketch, "E225.19.1", {"start": v(12.58, 130.96) * mm, "end": v(13.85, 131.23) * mm});
            skArc(sketch, "E225.19.2", {"start": v(11.27, 133.9) * mm, "mid": v(-17.7, 126.1) * mm, "end": v(11.27, 133.88) * mm});
            skArc(sketch, "E225.19.3", {"start": v(11.78, 130) * mm, "mid": v(-18.22, 130) * mm, "end": v(11.78, 129.98) * mm});
            skArc(sketch, "E225.19.4", {"start": v(14.63, 132.37) * mm, "mid": v(14.28, 133) * mm, "end": v(13.58, 133.23) * mm});
            skArc(sketch, "E225.19.5", {"start": v(11.27, 133.9) * mm, "mid": v(11.65, 133.35) * mm, "end": v(12.29, 133.16) * mm});
            skArc(sketch, "E225.19.6", {"start": v(14.63, 132.37) * mm, "mid": v(14.63, 132.35) * mm, "end": v(14.63, 132.33) * mm});
            skArc(sketch, "E225.19.7", {"start": v(12.58, 130.96) * mm, "mid": v(12, 130.6) * mm, "end": v(11.78, 129.98) * mm});
            skArc(sketch, "E225.19.8", {"start": v(13.85, 131.23) * mm, "mid": v(14.46, 131.63) * mm, "end": v(14.63, 132.33) * mm});
            skLineSegment(sketch, "E225.20.0", {"start": v(10.94, 137.07) * mm, "end": v(12.18, 137.47) * mm});
            skLineSegment(sketch, "E225.20.1", {"start": v(11.8, 135.01) * mm, "end": v(12.95, 135.6) * mm});
            skArc(sketch, "E225.20.2", {"start": v(9.77, 137.52) * mm, "mid": v(-16.2, 122.5) * mm, "end": v(9.78, 137.5) * mm});
            skArc(sketch, "E225.20.3", {"start": v(11.27, 133.88) * mm, "mid": v(-17.7, 126.13) * mm, "end": v(11.28, 133.86) * mm});
            skArc(sketch, "E225.20.4", {"start": v(13.4, 136.9) * mm, "mid": v(12.9, 137.43) * mm, "end": v(12.18, 137.47) * mm});
            skArc(sketch, "E225.20.5", {"start": v(9.77, 137.52) * mm, "mid": v(10.27, 137.08) * mm, "end": v(10.94, 137.07) * mm});
            skArc(sketch, "E225.20.6", {"start": v(13.4, 136.9) * mm, "mid": v(13.41, 136.89) * mm, "end": v(13.42, 136.87) * mm});
            skArc(sketch, "E225.20.7", {"start": v(11.8, 135.01) * mm, "mid": v(11.33, 134.53) * mm, "end": v(11.28, 133.86) * mm});
            skArc(sketch, "E225.20.8", {"start": v(12.95, 135.6) * mm, "mid": v(13.43, 136.14) * mm, "end": v(13.42, 136.87) * mm});
            skLineSegment(sketch, "E225.21.0", {"start": v(8.63, 140.5) * mm, "end": v(9.72, 141.2) * mm});
            skLineSegment(sketch, "E225.21.1", {"start": v(9.98, 138.73) * mm, "end": v(10.95, 139.6) * mm});
            skArc(sketch, "E225.21.2", {"start": v(7.38, 140.62) * mm, "mid": v(-13.81, 119.39) * mm, "end": v(7.4, 140.6) * mm});
            skArc(sketch, "E225.21.3", {"start": v(9.78, 137.5) * mm, "mid": v(-16.21, 122.5) * mm, "end": v(9.79, 137.48) * mm});
            skArc(sketch, "E225.21.4", {"start": v(11.06, 140.97) * mm, "mid": v(10.43, 141.35) * mm, "end": v(9.72, 141.2) * mm});
            skArc(sketch, "E225.21.5", {"start": v(7.38, 140.62) * mm, "mid": v(7.98, 140.33) * mm, "end": v(8.63, 140.5) * mm});
            skArc(sketch, "E225.21.6", {"start": v(11.06, 140.97) * mm, "mid": v(11.07, 140.96) * mm, "end": v(11.07, 140.95) * mm});
            skArc(sketch, "E225.21.7", {"start": v(9.98, 138.73) * mm, "mid": v(9.66, 138.14) * mm, "end": v(9.79, 137.48) * mm});
            skArc(sketch, "E225.21.8", {"start": v(10.95, 139.6) * mm, "mid": v(11.28, 140.24) * mm, "end": v(11.07, 140.95) * mm});
            skLineSegment(sketch, "E225.22.0", {"start": v(5.51, 143.2) * mm, "end": v(6.38, 144.16) * mm});
            skLineSegment(sketch, "E225.22.1", {"start": v(7.28, 141.84) * mm, "end": v(7.98, 142.93) * mm});
            skArc(sketch, "E225.22.2", {"start": v(4.27, 143) * mm, "mid": v(-10.7, 117) * mm, "end": v(4.28, 143) * mm});
            skArc(sketch, "E225.22.3", {"start": v(7.4, 140.6) * mm, "mid": v(-13.83, 119.4) * mm, "end": v(7.4, 140.6) * mm});
            skArc(sketch, "E225.22.4", {"start": v(7.73, 144.29) * mm, "mid": v(7.03, 144.5) * mm, "end": v(6.38, 144.16) * mm});
            skArc(sketch, "E225.22.5", {"start": v(4.27, 143) * mm, "mid": v(4.92, 142.88) * mm, "end": v(5.51, 143.2) * mm});
            skArc(sketch, "E225.22.6", {"start": v(7.73, 144.29) * mm, "mid": v(7.74, 144.28) * mm, "end": v(7.76, 144.27) * mm});
            skArc(sketch, "E225.22.7", {"start": v(7.28, 141.84) * mm, "mid": v(7.12, 141.2) * mm, "end": v(7.4, 140.6) * mm});
            skArc(sketch, "E225.22.8", {"start": v(7.98, 142.93) * mm, "mid": v(8.13, 143.65) * mm, "end": v(7.76, 144.27) * mm});
            skLineSegment(sketch, "E225.23.0", {"start": v(1.8, 145) * mm, "end": v(2.39, 146.16) * mm});
            skLineSegment(sketch, "E225.23.1", {"start": v(3.85, 144.16) * mm, "end": v(4.25, 145.4) * mm});
            skArc(sketch, "E225.23.2", {"start": v(0.65, 144.5) * mm, "mid": v(-7.09, 115.5) * mm, "end": v(0.67, 144.49) * mm});
            skArc(sketch, "E225.23.3", {"start": v(4.28, 143) * mm, "mid": v(-10.72, 117.01) * mm, "end": v(4.3, 142.98) * mm});
            skArc(sketch, "E225.23.4", {"start": v(3.66, 146.64) * mm, "mid": v(2.93, 146.65) * mm, "end": v(2.39, 146.16) * mm});
            skArc(sketch, "E225.23.5", {"start": v(0.65, 144.5) * mm, "mid": v(1.31, 144.55) * mm, "end": v(1.8, 145) * mm});
            skArc(sketch, "E225.23.6", {"start": v(3.66, 146.64) * mm, "mid": v(3.67, 146.63) * mm, "end": v(3.69, 146.62) * mm});
            skArc(sketch, "E225.23.7", {"start": v(3.85, 144.16) * mm, "mid": v(3.87, 143.49) * mm, "end": v(4.3, 142.98) * mm});
            skArc(sketch, "E225.23.8", {"start": v(4.25, 145.4) * mm, "mid": v(4.21, 146.12) * mm, "end": v(3.69, 146.62) * mm});
            skCircle(sketch, "E226", {"center": v(-3.22, 130) * mm, "radius": 1.6 * mm});
            skSolve(sketch);
        }
        {
            var Q0;
            Q0 = qSketchRegion(id + "F26", true);
            var Q1;
            Q1=makeQuery(id+"F26.imprint","IMPRINT",FACE,{"disambiguationData":[TD([[makeQuery(id+"F26.imprint","IMPRINT",EDGE,{"derivedFrom":sQuery(id+"F26.wireOp",EDGE,"E226")}),1.0]])]});
            var Q2;
            {var subQ9=sQuery(id+"F26.wireOp",EDGE,"E225.23.2");Q2=makeQuery(id+"F26.imprint","IMPRINT",FACE,{"disambiguationData":[TD([[makeQuery(id+"F26.imprint","IMPRINT",EDGE,{"derivedFrom":subQ9}),1.0]])]});}
            var Q3;
            {var subQ0=sQuery(id+"F26.wireOp",EDGE,"E225.23.3");var subQ17=makeQuery(id+"F26.imprint","IMPRINT",VERTEX,{"disambiguationData":[OD(8.0)],"derivedFrom":subQ0});Q3=makeQuery(id+"F26.imprint","IMPRINT",FACE,{"disambiguationData":[TD([[makeQuery(id+"F26.imprint","IMPRINT",EDGE,{"disambiguationData":[TD([[subQ17,1.0]])],"derivedFrom":subQ0}),1.0]])]});}
            extrude(context, id + "F27", {"entities" : qUnion([Q0, Q1, Q2, Q3]), "depth" : 3 * mm});
        }
    });
